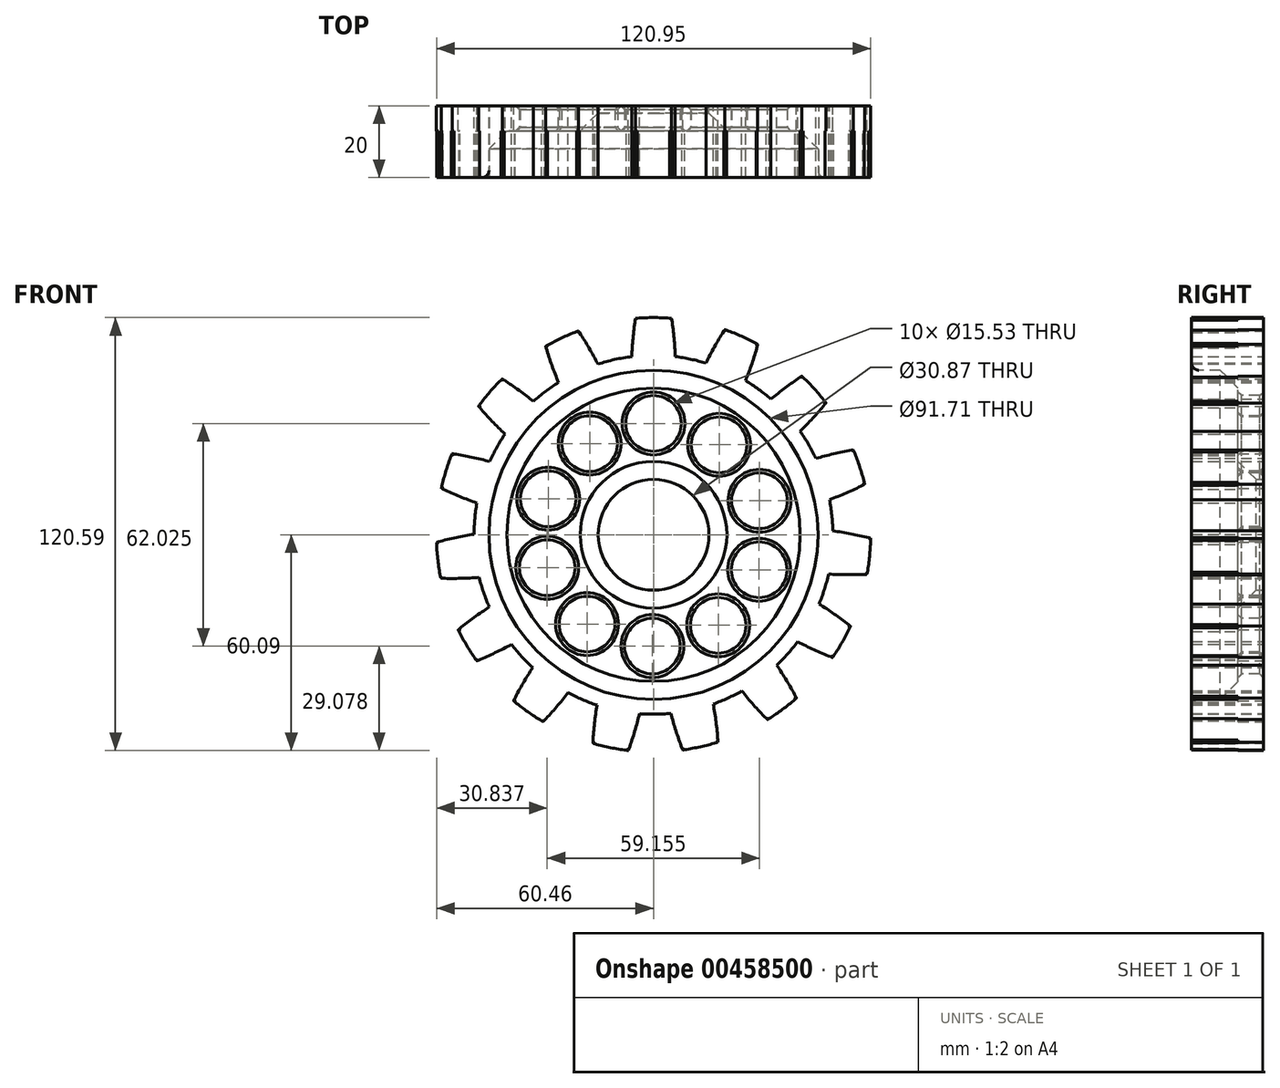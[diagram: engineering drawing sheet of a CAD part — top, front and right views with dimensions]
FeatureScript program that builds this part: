
annotation { "Feature Type Name" : "Feature", "Feature Type Description" : "" }
export const myFeature = defineFeature(function(context is Context, id is Id, definition is map)
    precondition{}
    {
        {
            var Q0;
            Q0=qCreatedBy(makeId("Front.planeOp"),FACE);
            var sketch = newSketch(context, id + "F0", { "sketchPlane" : qUnion([Q0])});
            skCircle(sketch, "E0", {"center": v(0, 0) * mm, "radius": 50 * mm});
            skArc(sketch, "E1", {"start": v(-2.05, -12.38) * mm, "mid": v(0, -12.55) * mm, "end": v(2.05, -12.38) * mm});
            skLineSegment(sketch, "E2.right", {"start": v(2.05, 10.3) * mm, "end": v(2.05, -12.38) * mm});
            skLineSegment(sketch, "E3.right", {"start": v(-2.05, 10.5) * mm, "end": v(-2.05, -12.38) * mm});
            skLineSegment(sketch, "E4", {"start": v(2.05, 10.3) * mm, "end": v(2.05, 12.38) * mm});
            skLineSegment(sketch, "E5", {"start": v(2.05, 12.38) * mm, "end": v(2.05, 10.3) * mm});
            skLineSegment(sketch, "E6", {"start": v(-2.05, 10.5) * mm, "end": v(-2.05, 12.38) * mm});
            skPoint(sketch, "E7.orphan", {"position": v(0, 10.5) * mm});
            skArc(sketch, "E8.trimOffspring", {"start": v(2.05, 12.38) * mm, "mid": v(0, 12.55) * mm, "end": v(-2.05, 12.38) * mm});
            skLineSegment(sketch, "E9.1.0", {"start": v(-7.83, 7.29) * mm, "end": v(5.62, -11.22) * mm});
            skLineSegment(sketch, "E9.1.1", {"start": v(-7.83, 7.29) * mm, "end": v(-8.94, 8.81) * mm});
            skArc(sketch, "E9.1.2", {"start": v(-5.62, 11.22) * mm, "mid": v(-7.38, 10.15) * mm, "end": v(-8.94, 8.81) * mm});
            skLineSegment(sketch, "E9.1.3", {"start": v(-4.4, 9.54) * mm, "end": v(8.94, -8.81) * mm});
            skLineSegment(sketch, "E9.1.4", {"start": v(-5.62, 11.22) * mm, "end": v(-4.4, 9.54) * mm});
            skArc(sketch, "E9.1.5", {"start": v(5.62, -11.22) * mm, "mid": v(7.38, -10.15) * mm, "end": v(8.94, -8.81) * mm});
            skLineSegment(sketch, "E9.2.0", {"start": v(-10.62, 1.3) * mm, "end": v(11.14, -5.78) * mm});
            skLineSegment(sketch, "E9.2.1", {"start": v(-10.62, 1.3) * mm, "end": v(-12.4, 1.88) * mm});
            skArc(sketch, "E9.2.2", {"start": v(-11.14, 5.78) * mm, "mid": v(-11.94, 3.88) * mm, "end": v(-12.4, 1.88) * mm});
            skLineSegment(sketch, "E9.2.3", {"start": v(-9.16, 5.13) * mm, "end": v(12.4, -1.88) * mm});
            skLineSegment(sketch, "E9.2.4", {"start": v(-11.14, 5.78) * mm, "end": v(-9.16, 5.13) * mm});
            skArc(sketch, "E9.2.5", {"start": v(11.14, -5.78) * mm, "mid": v(11.94, -3.88) * mm, "end": v(12.4, -1.88) * mm});
            skLineSegment(sketch, "E9.3.0", {"start": v(-9.35, -5.2) * mm, "end": v(12.4, 1.88) * mm});
            skLineSegment(sketch, "E9.3.1", {"start": v(-9.35, -5.2) * mm, "end": v(-11.14, -5.78) * mm});
            skArc(sketch, "E9.3.2", {"start": v(-12.4, -1.88) * mm, "mid": v(-11.94, -3.88) * mm, "end": v(-11.14, -5.78) * mm});
            skLineSegment(sketch, "E9.3.3", {"start": v(-10.43, -1.23) * mm, "end": v(11.14, 5.78) * mm});
            skLineSegment(sketch, "E9.3.4", {"start": v(-12.4, -1.88) * mm, "end": v(-10.43, -1.23) * mm});
            skArc(sketch, "E9.3.5", {"start": v(12.4, 1.88) * mm, "mid": v(11.94, 3.88) * mm, "end": v(11.14, 5.78) * mm});
            skLineSegment(sketch, "E9.4.0", {"start": v(-4.51, -9.7) * mm, "end": v(8.94, 8.81) * mm});
            skLineSegment(sketch, "E9.4.1", {"start": v(-4.51, -9.7) * mm, "end": v(-5.62, -11.22) * mm});
            skArc(sketch, "E9.4.2", {"start": v(-8.94, -8.81) * mm, "mid": v(-7.38, -10.15) * mm, "end": v(-5.62, -11.22) * mm});
            skLineSegment(sketch, "E9.4.3", {"start": v(-7.71, -7.13) * mm, "end": v(5.62, 11.22) * mm});
            skLineSegment(sketch, "E9.4.4", {"start": v(-8.94, -8.81) * mm, "end": v(-7.71, -7.13) * mm});
            skArc(sketch, "E9.4.5", {"start": v(8.94, 8.81) * mm, "mid": v(7.38, 10.15) * mm, "end": v(5.62, 11.22) * mm});
            skLineSegment(sketch, "E9.5.0", {"start": v(2.05, -10.5) * mm, "end": v(2.05, 12.38) * mm});
            skLineSegment(sketch, "E9.5.1", {"start": v(2.05, -10.5) * mm, "end": v(2.05, -12.38) * mm});
            skLineSegment(sketch, "E9.5.3", {"start": v(-2.05, -10.3) * mm, "end": v(-2.05, 12.38) * mm});
            skLineSegment(sketch, "E9.5.4", {"start": v(-2.05, -12.38) * mm, "end": v(-2.05, -10.3) * mm});
            skLineSegment(sketch, "E9.6.0", {"start": v(7.83, -7.29) * mm, "end": v(-5.62, 11.22) * mm});
            skLineSegment(sketch, "E9.6.1", {"start": v(7.83, -7.29) * mm, "end": v(8.94, -8.81) * mm});
            skArc(sketch, "E9.6.2", {"start": v(5.62, -11.22) * mm, "mid": v(7.38, -10.15) * mm, "end": v(8.94, -8.81) * mm});
            skLineSegment(sketch, "E9.6.3", {"start": v(4.4, -9.54) * mm, "end": v(-8.94, 8.81) * mm});
            skLineSegment(sketch, "E9.6.4", {"start": v(5.62, -11.22) * mm, "end": v(4.4, -9.54) * mm});
            skArc(sketch, "E9.6.5", {"start": v(-5.62, 11.22) * mm, "mid": v(-7.38, 10.15) * mm, "end": v(-8.94, 8.81) * mm});
            skLineSegment(sketch, "E9.7.0", {"start": v(10.62, -1.3) * mm, "end": v(-11.14, 5.78) * mm});
            skLineSegment(sketch, "E9.7.1", {"start": v(10.62, -1.3) * mm, "end": v(12.4, -1.88) * mm});
            skArc(sketch, "E9.7.2", {"start": v(11.14, -5.78) * mm, "mid": v(11.94, -3.88) * mm, "end": v(12.4, -1.88) * mm});
            skLineSegment(sketch, "E9.7.3", {"start": v(9.16, -5.13) * mm, "end": v(-12.4, 1.88) * mm});
            skLineSegment(sketch, "E9.7.4", {"start": v(11.14, -5.78) * mm, "end": v(9.16, -5.13) * mm});
            skArc(sketch, "E9.7.5", {"start": v(-11.14, 5.78) * mm, "mid": v(-11.94, 3.88) * mm, "end": v(-12.4, 1.88) * mm});
            skLineSegment(sketch, "E9.8.0", {"start": v(9.35, 5.2) * mm, "end": v(-12.4, -1.88) * mm});
            skLineSegment(sketch, "E9.8.1", {"start": v(9.35, 5.2) * mm, "end": v(11.14, 5.78) * mm});
            skArc(sketch, "E9.8.2", {"start": v(12.4, 1.88) * mm, "mid": v(11.94, 3.88) * mm, "end": v(11.14, 5.78) * mm});
            skLineSegment(sketch, "E9.8.3", {"start": v(10.43, 1.23) * mm, "end": v(-11.14, -5.78) * mm});
            skLineSegment(sketch, "E9.8.4", {"start": v(12.4, 1.88) * mm, "end": v(10.43, 1.23) * mm});
            skArc(sketch, "E9.8.5", {"start": v(-12.4, -1.88) * mm, "mid": v(-11.94, -3.88) * mm, "end": v(-11.14, -5.78) * mm});
            skLineSegment(sketch, "E9.9.0", {"start": v(4.51, 9.7) * mm, "end": v(-8.94, -8.81) * mm});
            skLineSegment(sketch, "E9.9.1", {"start": v(4.51, 9.7) * mm, "end": v(5.62, 11.22) * mm});
            skArc(sketch, "E9.9.2", {"start": v(8.94, 8.81) * mm, "mid": v(7.38, 10.15) * mm, "end": v(5.62, 11.22) * mm});
            skLineSegment(sketch, "E9.9.3", {"start": v(7.71, 7.13) * mm, "end": v(-5.62, -11.22) * mm});
            skLineSegment(sketch, "E9.9.4", {"start": v(8.94, 8.81) * mm, "end": v(7.71, 7.13) * mm});
            skArc(sketch, "E9.9.5", {"start": v(-8.94, -8.81) * mm, "mid": v(-7.38, -10.15) * mm, "end": v(-5.62, -11.22) * mm});
            skLineSegment(sketch, "E10", {"start": v(0, 50) * mm, "end": v(0, 46.5) * mm, "construction": true});
            skLineSegment(sketch, "E11", {"start": v(0, 46.5) * mm, "end": v(83.9, 46.5) * mm, "construction": true});
            skArc(sketch, "E12", {"start": v(-5.04, 60.29) * mm, "mid": v(-5.7, 54.98) * mm, "end": v(-6.05, 49.63) * mm});
            skArc(sketch, "E13", {"start": v(5.04, 60.29) * mm, "mid": v(0, 60.5) * mm, "end": v(-5.04, 60.29) * mm});
            skArc(sketch, "E14.MirrorC", {"start": v(5.04, 60.29) * mm, "mid": v(5.83, 53.42) * mm, "end": v(6.1, 46.5) * mm});
            skArc(sketch, "E15.trimOffspring", {"start": v(-6.8, 0.06) * mm, "mid": v(-6.85, -0.01) * mm, "end": v(-6.9, -0.08) * mm});
            skArc(sketch, "E16.trimOffspring", {"start": v(4.73, 3.7) * mm, "mid": v(4.84, 3.5) * mm, "end": v(4.94, 3.31) * mm});
            skArc(sketch, "E17.trimOffspring", {"start": v(6.8, 0.06) * mm, "mid": v(6.85, -0.01) * mm, "end": v(6.9, -0.08) * mm});
            skArc(sketch, "E18.1.0", {"start": v(29.06, 53.07) * mm, "mid": v(24.54, 55.3) * mm, "end": v(19.85, 57.15) * mm});
            skArc(sketch, "E18.1.1", {"start": v(19.85, 57.15) * mm, "mid": v(17.09, 52.56) * mm, "end": v(14.6, 47.82) * mm});
            skArc(sketch, "E18.1.2", {"start": v(29.06, 53.07) * mm, "mid": v(27, 46.46) * mm, "end": v(24.44, 40.03) * mm});
            skArc(sketch, "E18.2.0", {"start": v(48.08, 36.72) * mm, "mid": v(44.86, 40.6) * mm, "end": v(41.32, 44.19) * mm});
            skArc(sketch, "E18.2.1", {"start": v(41.32, 44.19) * mm, "mid": v(36.94, 41.11) * mm, "end": v(32.75, 37.79) * mm});
            skArc(sketch, "E18.2.2", {"start": v(48.08, 36.72) * mm, "mid": v(43.52, 31.52) * mm, "end": v(38.57, 26.68) * mm});
            skArc(sketch, "E18.3.0", {"start": v(58.84, 14.06) * mm, "mid": v(57.47, 18.91) * mm, "end": v(55.7, 23.63) * mm});
            skArc(sketch, "E18.3.1", {"start": v(55.7, 23.63) * mm, "mid": v(50.44, 22.6) * mm, "end": v(45.26, 21.26) * mm});
            skArc(sketch, "E18.3.2", {"start": v(58.84, 14.06) * mm, "mid": v(52.56, 11.15) * mm, "end": v(46.08, 8.74) * mm});
            skArc(sketch, "E18.4.0", {"start": v(59.49, -11.02) * mm, "mid": v(60.2, -6.02) * mm, "end": v(60.5, -1) * mm});
            skArc(sketch, "E18.4.1", {"start": v(60.5, -1) * mm, "mid": v(55.27, 0.2) * mm, "end": v(49.99, 1.07) * mm});
            skArc(sketch, "E18.4.2", {"start": v(59.49, -11.02) * mm, "mid": v(52.57, -11.12) * mm, "end": v(45.66, -10.7) * mm});
            skArc(sketch, "E18.5.0", {"start": v(49.9, -34.2) * mm, "mid": v(52.58, -29.92) * mm, "end": v(54.9, -25.44) * mm});
            skArc(sketch, "E18.5.1", {"start": v(54.9, -25.44) * mm, "mid": v(50.6, -22.24) * mm, "end": v(46.13, -19.3) * mm});
            skArc(sketch, "E18.5.2", {"start": v(49.9, -34.2) * mm, "mid": v(43.54, -31.49) * mm, "end": v(37.4, -28.3) * mm});
            skArc(sketch, "E18.6.0", {"start": v(31.75, -51.5) * mm, "mid": v(35.93, -48.68) * mm, "end": v(39.85, -45.52) * mm});
            skArc(sketch, "E18.6.1", {"start": v(39.85, -45.52) * mm, "mid": v(37.23, -40.85) * mm, "end": v(34.34, -36.34) * mm});
            skArc(sketch, "E18.6.2", {"start": v(31.75, -51.5) * mm, "mid": v(27.03, -46.44) * mm, "end": v(22.7, -41.04) * mm});
            skArc(sketch, "E18.7.0", {"start": v(8.13, -59.95) * mm, "mid": v(13.1, -59.07) * mm, "end": v(17.97, -57.77) * mm});
            skArc(sketch, "E18.7.1", {"start": v(17.97, -57.77) * mm, "mid": v(17.46, -52.44) * mm, "end": v(16.64, -47.15) * mm});
            skArc(sketch, "E18.7.2", {"start": v(8.13, -59.95) * mm, "mid": v(5.87, -53.41) * mm, "end": v(4.1, -46.72) * mm});
            skArc(sketch, "E18.8.0", {"start": v(-16.88, -58.1) * mm, "mid": v(-11.99, -59.3) * mm, "end": v(-7, -60.1) * mm});
            skArc(sketch, "E18.8.1", {"start": v(-7, -60.1) * mm, "mid": v(-5.3, -55.02) * mm, "end": v(-3.9, -49.85) * mm});
            skArc(sketch, "E18.8.2", {"start": v(-16.88, -58.1) * mm, "mid": v(-16.3, -51.2) * mm, "end": v(-15.2, -44.37) * mm});
            skArc(sketch, "E18.9.0", {"start": v(-39, -46.26) * mm, "mid": v(-35, -49.34) * mm, "end": v(-30.78, -52.09) * mm});
            skArc(sketch, "E18.9.1", {"start": v(-30.78, -52.09) * mm, "mid": v(-27.16, -48.14) * mm, "end": v(-23.8, -43.98) * mm});
            skArc(sketch, "E18.9.2", {"start": v(-39, -46.26) * mm, "mid": v(-35.67, -40.19) * mm, "end": v(-31.88, -34.4) * mm});
            skArc(sketch, "E18.10.0", {"start": v(-54.4, -26.46) * mm, "mid": v(-52.01, -30.9) * mm, "end": v(-49.26, -35.12) * mm});
            skArc(sketch, "E18.10.1", {"start": v(-49.26, -35.12) * mm, "mid": v(-44.35, -32.98) * mm, "end": v(-39.58, -30.55) * mm});
            skArc(sketch, "E18.10.2", {"start": v(-54.4, -26.46) * mm, "mid": v(-48.9, -22.27) * mm, "end": v(-43.1, -18.5) * mm});
            skArc(sketch, "E18.11.0", {"start": v(-60.46, -2.12) * mm, "mid": v(-60.08, -7.15) * mm, "end": v(-59.27, -12.13) * mm});
            skArc(sketch, "E18.11.1", {"start": v(-59.27, -12.13) * mm, "mid": v(-53.92, -12.16) * mm, "end": v(-48.57, -11.87) * mm});
            skArc(sketch, "E18.11.2", {"start": v(-60.46, -2.12) * mm, "mid": v(-53.73, -0.52) * mm, "end": v(-46.9, 0.56) * mm});
            skArc(sketch, "E18.12.0", {"start": v(-56.13, 22.58) * mm, "mid": v(-57.81, 17.83) * mm, "end": v(-59.1, 12.96) * mm});
            skArc(sketch, "E18.12.1", {"start": v(-59.1, 12.96) * mm, "mid": v(-54.21, 10.76) * mm, "end": v(-49.21, 8.85) * mm});
            skArc(sketch, "E18.12.2", {"start": v(-56.13, 22.58) * mm, "mid": v(-49.32, 21.32) * mm, "end": v(-42.64, 19.54) * mm});
            skArc(sketch, "E18.13.0", {"start": v(-42.14, 43.4) * mm, "mid": v(-45.61, 39.75) * mm, "end": v(-48.76, 35.81) * mm});
            skArc(sketch, "E18.13.1", {"start": v(-48.76, 35.81) * mm, "mid": v(-45.2, 31.82) * mm, "end": v(-41.39, 28.05) * mm});
            skArc(sketch, "E18.13.2", {"start": v(-42.14, 43.4) * mm, "mid": v(-36.44, 39.5) * mm, "end": v(-31.05, 35.15) * mm});
            skArc(sketch, "E18.14.0", {"start": v(-20.91, 56.77) * mm, "mid": v(-25.57, 54.83) * mm, "end": v(-30.04, 52.51) * mm});
            skArc(sketch, "E18.14.1", {"start": v(-30.04, 52.51) * mm, "mid": v(-28.4, 47.42) * mm, "end": v(-26.45, 42.43) * mm});
            skArc(sketch, "E18.14.2", {"start": v(-20.91, 56.77) * mm, "mid": v(-17.29, 50.88) * mm, "end": v(-14.12, 44.72) * mm});
            skLineSegment(sketch, "E18.anchor1", {"start": v(0, 0) * mm, "end": v(-5.04, 60.29) * mm, "construction": true});
            skLineSegment(sketch, "E18.anchor2", {"start": v(0, 0) * mm, "end": v(-30.04, 52.51) * mm, "construction": true});
            skCircle(sketch, "E19", {"center": v(0, 0) * mm, "radius": 10.5 * mm});
            skCircle(sketch, "E20", {"center": v(0, 0) * mm, "radius": 15.43 * mm});
            skSolve(sketch);
        }
        {
            var Q0;
            {var subQ0=sQuery(id+"F0.wireOp",EDGE,"E12");Q0=makeQuery(id+"F0.imprint","IMPRINT",FACE,{"disambiguationData":[TD([[makeQuery(id+"F0.imprint","IMPRINT",EDGE,{"derivedFrom":subQ0}),1.0]])]});}
            var Q1;
            {var subQ4=sQuery(id+"F0.wireOp",EDGE,"E18.14.0");Q1=makeQuery(id+"F0.imprint","IMPRINT",FACE,{"disambiguationData":[TD([[makeQuery(id+"F0.imprint","IMPRINT",EDGE,{"derivedFrom":subQ4}),1.0]])]});}
            var Q2;
            {var subQ4=sQuery(id+"F0.wireOp",EDGE,"E18.13.0");Q2=makeQuery(id+"F0.imprint","IMPRINT",FACE,{"disambiguationData":[TD([[makeQuery(id+"F0.imprint","IMPRINT",EDGE,{"derivedFrom":subQ4}),1.0]])]});}
            var Q3;
            {var subQ4=sQuery(id+"F0.wireOp",EDGE,"E18.12.0");Q3=makeQuery(id+"F0.imprint","IMPRINT",FACE,{"disambiguationData":[TD([[makeQuery(id+"F0.imprint","IMPRINT",EDGE,{"derivedFrom":subQ4}),1.0]])]});}
            var Q4;
            {var subQ4=sQuery(id+"F0.wireOp",EDGE,"E18.11.0");Q4=makeQuery(id+"F0.imprint","IMPRINT",FACE,{"disambiguationData":[TD([[makeQuery(id+"F0.imprint","IMPRINT",EDGE,{"derivedFrom":subQ4}),1.0]])]});}
            var Q5;
            {var subQ4=sQuery(id+"F0.wireOp",EDGE,"E18.10.0");Q5=makeQuery(id+"F0.imprint","IMPRINT",FACE,{"disambiguationData":[TD([[makeQuery(id+"F0.imprint","IMPRINT",EDGE,{"derivedFrom":subQ4}),1.0]])]});}
            var Q6;
            {var subQ4=sQuery(id+"F0.wireOp",EDGE,"E18.9.0");Q6=makeQuery(id+"F0.imprint","IMPRINT",FACE,{"disambiguationData":[TD([[makeQuery(id+"F0.imprint","IMPRINT",EDGE,{"derivedFrom":subQ4}),1.0]])]});}
            var Q7;
            {var subQ4=sQuery(id+"F0.wireOp",EDGE,"E18.8.0");Q7=makeQuery(id+"F0.imprint","IMPRINT",FACE,{"disambiguationData":[TD([[makeQuery(id+"F0.imprint","IMPRINT",EDGE,{"derivedFrom":subQ4}),1.0]])]});}
            var Q8;
            {var subQ4=sQuery(id+"F0.wireOp",EDGE,"E18.7.0");Q8=makeQuery(id+"F0.imprint","IMPRINT",FACE,{"disambiguationData":[TD([[makeQuery(id+"F0.imprint","IMPRINT",EDGE,{"derivedFrom":subQ4}),1.0]])]});}
            var Q9;
            {var subQ4=sQuery(id+"F0.wireOp",EDGE,"E18.5.0");Q9=makeQuery(id+"F0.imprint","IMPRINT",FACE,{"disambiguationData":[TD([[makeQuery(id+"F0.imprint","IMPRINT",EDGE,{"derivedFrom":subQ4}),1.0]])]});}
            var Q10;
            {var subQ4=sQuery(id+"F0.wireOp",EDGE,"E18.4.0");Q10=makeQuery(id+"F0.imprint","IMPRINT",FACE,{"disambiguationData":[TD([[makeQuery(id+"F0.imprint","IMPRINT",EDGE,{"derivedFrom":subQ4}),1.0]])]});}
            var Q11;
            {var subQ4=sQuery(id+"F0.wireOp",EDGE,"E18.3.0");Q11=makeQuery(id+"F0.imprint","IMPRINT",FACE,{"disambiguationData":[TD([[makeQuery(id+"F0.imprint","IMPRINT",EDGE,{"derivedFrom":subQ4}),1.0]])]});}
            var Q12;
            {var subQ4=sQuery(id+"F0.wireOp",EDGE,"E18.2.0");Q12=makeQuery(id+"F0.imprint","IMPRINT",FACE,{"disambiguationData":[TD([[makeQuery(id+"F0.imprint","IMPRINT",EDGE,{"derivedFrom":subQ4}),1.0]])]});}
            var Q13;
            {var subQ4=sQuery(id+"F0.wireOp",EDGE,"E18.1.0");Q13=makeQuery(id+"F0.imprint","IMPRINT",FACE,{"disambiguationData":[TD([[makeQuery(id+"F0.imprint","IMPRINT",EDGE,{"derivedFrom":subQ4}),1.0]])]});}
            var Q14;
            {var subQ4=sQuery(id+"F0.wireOp",EDGE,"E18.6.0");Q14=makeQuery(id+"F0.imprint","IMPRINT",FACE,{"disambiguationData":[TD([[makeQuery(id+"F0.imprint","IMPRINT",EDGE,{"derivedFrom":subQ4}),1.0]])]});}
            var Q15;
            {var subQ8=sQuery(id+"F0.wireOp",EDGE,"E9.5.1");Q15=makeQuery(id+"F0.imprint","IMPRINT",FACE,{"disambiguationData":[TD([[makeQuery(id+"F0.imprint","IMPRINT",EDGE,{"derivedFrom":subQ8}),1.0]])]});}
            var Q16;
            Q16=makeQuery(id+"F0.imprint","IMPRINT",FACE,{"disambiguationData":[TD([[makeQuery(id+"F0.imprint","IMPRINT",EDGE,{"derivedFrom":sQuery(id+"F0.wireOp",EDGE,"E20")}),-1.0]])]});
            extrude(context, id + "F1", {"entities" : qUnion([Q0, Q1, Q2, Q3, Q4, Q5, Q6, Q7, Q8, Q9, Q10, Q11, Q12, Q13, Q14, Q15, Q16]), "depth" : 20 * mm});
        }
        {
            var Q0;
            Q0=makeQuery(id+"F1.opExtrude","SWEPT_EDGE",EDGE,{"disambiguationData":[OSD([sQuery(id+"F0.wireOp",EDGE,"E12"),sQuery(id+"F0.wireOp",EDGE,"E13")])]});
            var Q1;
            Q1=makeQuery(id+"F1.opExtrude","SWEPT_EDGE",EDGE,{"disambiguationData":[OSD([sQuery(id+"F0.wireOp",EDGE,"E13"),sQuery(id+"F0.wireOp",EDGE,"E14.MirrorC")])]});
            var Q2;
            Q2=makeQuery(id+"F1.opExtrude","SWEPT_EDGE",EDGE,{"disambiguationData":[OSD([sQuery(id+"F0.wireOp",EDGE,"E18.14.0"),sQuery(id+"F0.wireOp",EDGE,"E18.14.2")])]});
            var Q3;
            Q3=makeQuery(id+"F1.opExtrude","SWEPT_EDGE",EDGE,{"disambiguationData":[OSD([sQuery(id+"F0.wireOp",EDGE,"E18.14.0"),sQuery(id+"F0.wireOp",EDGE,"E18.14.1")])]});
            var Q4;
            Q4=makeQuery(id+"F1.opExtrude","SWEPT_EDGE",EDGE,{"disambiguationData":[OSD([sQuery(id+"F0.wireOp",EDGE,"E18.13.0"),sQuery(id+"F0.wireOp",EDGE,"E18.13.2")])]});
            var Q5;
            Q5=makeQuery(id+"F1.opExtrude","SWEPT_EDGE",EDGE,{"disambiguationData":[OSD([sQuery(id+"F0.wireOp",EDGE,"E18.13.0"),sQuery(id+"F0.wireOp",EDGE,"E18.13.1")])]});
            var Q6;
            Q6=makeQuery(id+"F1.opExtrude","SWEPT_EDGE",EDGE,{"disambiguationData":[OSD([sQuery(id+"F0.wireOp",EDGE,"E18.12.0"),sQuery(id+"F0.wireOp",EDGE,"E18.12.2")])]});
            var Q7;
            Q7=makeQuery(id+"F1.opExtrude","SWEPT_EDGE",EDGE,{"disambiguationData":[OSD([sQuery(id+"F0.wireOp",EDGE,"E18.12.0"),sQuery(id+"F0.wireOp",EDGE,"E18.12.1")])]});
            var Q8;
            Q8=makeQuery(id+"F1.opExtrude","SWEPT_EDGE",EDGE,{"disambiguationData":[OSD([sQuery(id+"F0.wireOp",EDGE,"E18.1.0"),sQuery(id+"F0.wireOp",EDGE,"E18.1.1")])]});
            var Q9;
            Q9=makeQuery(id+"F1.opExtrude","SWEPT_EDGE",EDGE,{"disambiguationData":[OSD([sQuery(id+"F0.wireOp",EDGE,"E18.1.0"),sQuery(id+"F0.wireOp",EDGE,"E18.1.2")])]});
            var Q10;
            Q10=makeQuery(id+"F1.opExtrude","SWEPT_EDGE",EDGE,{"disambiguationData":[OSD([sQuery(id+"F0.wireOp",EDGE,"E18.2.0"),sQuery(id+"F0.wireOp",EDGE,"E18.2.1")])]});
            var Q11;
            Q11=makeQuery(id+"F1.opExtrude","SWEPT_EDGE",EDGE,{"disambiguationData":[OSD([sQuery(id+"F0.wireOp",EDGE,"E18.2.0"),sQuery(id+"F0.wireOp",EDGE,"E18.2.2")])]});
            var Q12;
            Q12=makeQuery(id+"F1.opExtrude","SWEPT_EDGE",EDGE,{"disambiguationData":[OSD([sQuery(id+"F0.wireOp",EDGE,"E18.3.0"),sQuery(id+"F0.wireOp",EDGE,"E18.3.1")])]});
            var Q13;
            Q13=makeQuery(id+"F1.opExtrude","SWEPT_EDGE",EDGE,{"disambiguationData":[OSD([sQuery(id+"F0.wireOp",EDGE,"E18.3.0"),sQuery(id+"F0.wireOp",EDGE,"E18.3.2")])]});
            var Q14;
            Q14=makeQuery(id+"F1.opExtrude","SWEPT_EDGE",EDGE,{"disambiguationData":[OSD([sQuery(id+"F0.wireOp",EDGE,"E18.4.0"),sQuery(id+"F0.wireOp",EDGE,"E18.4.1")])]});
            var Q15;
            Q15=makeQuery(id+"F1.opExtrude","SWEPT_EDGE",EDGE,{"disambiguationData":[OSD([sQuery(id+"F0.wireOp",EDGE,"E18.4.0"),sQuery(id+"F0.wireOp",EDGE,"E18.4.2")])]});
            var Q16;
            Q16=makeQuery(id+"F1.opExtrude","SWEPT_EDGE",EDGE,{"disambiguationData":[OSD([sQuery(id+"F0.wireOp",EDGE,"E18.5.0"),sQuery(id+"F0.wireOp",EDGE,"E18.5.1")])]});
            var Q17;
            Q17=makeQuery(id+"F1.opExtrude","SWEPT_EDGE",EDGE,{"disambiguationData":[OSD([sQuery(id+"F0.wireOp",EDGE,"E18.5.0"),sQuery(id+"F0.wireOp",EDGE,"E18.5.2")])]});
            var Q18;
            Q18=makeQuery(id+"F1.opExtrude","SWEPT_EDGE",EDGE,{"disambiguationData":[OSD([sQuery(id+"F0.wireOp",EDGE,"E18.6.0"),sQuery(id+"F0.wireOp",EDGE,"E18.6.1")])]});
            var Q19;
            Q19=makeQuery(id+"F1.opExtrude","SWEPT_EDGE",EDGE,{"disambiguationData":[OSD([sQuery(id+"F0.wireOp",EDGE,"E18.6.0"),sQuery(id+"F0.wireOp",EDGE,"E18.6.2")])]});
            var Q20;
            Q20=makeQuery(id+"F1.opExtrude","SWEPT_EDGE",EDGE,{"disambiguationData":[OSD([sQuery(id+"F0.wireOp",EDGE,"E18.7.0"),sQuery(id+"F0.wireOp",EDGE,"E18.7.1")])]});
            var Q21;
            Q21=makeQuery(id+"F1.opExtrude","SWEPT_EDGE",EDGE,{"disambiguationData":[OSD([sQuery(id+"F0.wireOp",EDGE,"E18.7.0"),sQuery(id+"F0.wireOp",EDGE,"E18.7.2")])]});
            var Q22;
            Q22=makeQuery(id+"F1.opExtrude","SWEPT_EDGE",EDGE,{"disambiguationData":[OSD([sQuery(id+"F0.wireOp",EDGE,"E18.8.0"),sQuery(id+"F0.wireOp",EDGE,"E18.8.1")])]});
            var Q23;
            Q23=makeQuery(id+"F1.opExtrude","SWEPT_EDGE",EDGE,{"disambiguationData":[OSD([sQuery(id+"F0.wireOp",EDGE,"E18.8.0"),sQuery(id+"F0.wireOp",EDGE,"E18.8.2")])]});
            var Q24;
            Q24=makeQuery(id+"F1.opExtrude","SWEPT_EDGE",EDGE,{"disambiguationData":[OSD([sQuery(id+"F0.wireOp",EDGE,"E18.11.0"),sQuery(id+"F0.wireOp",EDGE,"E18.11.2")])]});
            var Q25;
            Q25=makeQuery(id+"F1.opExtrude","SWEPT_EDGE",EDGE,{"disambiguationData":[OSD([sQuery(id+"F0.wireOp",EDGE,"E18.11.0"),sQuery(id+"F0.wireOp",EDGE,"E18.11.1")])]});
            var Q26;
            Q26=makeQuery(id+"F1.opExtrude","SWEPT_EDGE",EDGE,{"disambiguationData":[OSD([sQuery(id+"F0.wireOp",EDGE,"E18.10.0"),sQuery(id+"F0.wireOp",EDGE,"E18.10.2")])]});
            var Q27;
            Q27=makeQuery(id+"F1.opExtrude","SWEPT_EDGE",EDGE,{"disambiguationData":[OSD([sQuery(id+"F0.wireOp",EDGE,"E18.10.0"),sQuery(id+"F0.wireOp",EDGE,"E18.10.1")])]});
            var Q28;
            Q28=makeQuery(id+"F1.opExtrude","SWEPT_EDGE",EDGE,{"disambiguationData":[OSD([sQuery(id+"F0.wireOp",EDGE,"E18.9.0"),sQuery(id+"F0.wireOp",EDGE,"E18.9.2")])]});
            var Q29;
            Q29=makeQuery(id+"F1.opExtrude","SWEPT_EDGE",EDGE,{"disambiguationData":[OSD([sQuery(id+"F0.wireOp",EDGE,"E18.9.0"),sQuery(id+"F0.wireOp",EDGE,"E18.9.1")])]});
            chamfer(context, id + "F2", {"entities" : qUnion([Q0, Q1, Q2, Q3, Q4, Q5, Q6, Q7, Q8, Q9, Q10, Q11, Q12, Q13, Q14, Q15, Q16, Q17, Q18, Q19, Q20, Q21, Q22, Q23, Q24, Q25, Q26, Q27, Q28, Q29]), "width" : 0.7 * mm, "tangentPropagation" : true});
        }
        {
            var Q0;
            Q0=qCreatedBy(makeId("Front.planeOp"),FACE);
            cPlane(context, id + "F3", {"entities" : qUnion([Q0]), "cplaneType" : CPlaneType.OFFSET, "offset" : 21 * mm, "width" : 150 * mm, "height" : 150 * mm});
        }
        {
            var Q0;
            Q0=qCreatedBy(id+"F3.planeOp",FACE);
            var sketch = newSketch(context, id + "F4", { "sketchPlane" : qUnion([Q0])});
            skCircle(sketch, "E21", {"center": v(0, 0) * mm, "radius": 45.85 * mm});
            skSolve(sketch);
        }
        {
            var Q0;
            Q0=makeQuery(id+"F4.imprint","IMPRINT",FACE,{"disambiguationData":[TD([[makeQuery(id+"F4.imprint","IMPRINT",EDGE,{"derivedFrom":sQuery(id+"F4.wireOp",EDGE,"E21")}),1.0]])]});
            extrude(context, id + "F5", {"entities" : qUnion([Q0]), "operationType" : NewBodyOperationType.REMOVE, "oppositeDirection" : true, "depth" : 17 * mm});
        }
        {
            var Q0;
            Q0 = qSketchRegion(id + "F0", true);
            extrude(context, id + "F6", {"entities" : qUnion([Q0]), "operationType" : NewBodyOperationType.ADD, "depth" : 7 * mm});
        }
        {
            var Q0;
            {var subQ0=sQuery(id+"F0.wireOp",EDGE,"E20");Q0=makeQuery(id+"F6.boolean.opBoolean","SPLIT",FACE,{"disambiguationData":[TD([makeQuery(id+"F5.boolean.opBoolean","COPY",FACE,{"derivedFrom":makeQuery(id+"F5.opExtrude","SWEPT_FACE",FACE,{"disambiguationData":[OSD([sQuery(id+"F4.wireOp",EDGE,"E21")])]})})])],"derivedFrom":makeQuery(id+"F6.opExtrude","CAP_FACE",FACE,{"disambiguationData":[OSD([sQuery(id+"F0.wireOp",EDGE,"E0"),sQuery(id+"F0.wireOp",EDGE,"E12"),sQuery(id+"F0.wireOp",EDGE,"E13"),sQuery(id+"F0.wireOp",EDGE,"E14.MirrorC"),sQuery(id+"F0.wireOp",EDGE,"E18.1.0"),sQuery(id+"F0.wireOp",EDGE,"E18.1.1"),sQuery(id+"F0.wireOp",EDGE,"E18.1.2"),sQuery(id+"F0.wireOp",EDGE,"E18.2.0"),sQuery(id+"F0.wireOp",EDGE,"E18.2.1"),sQuery(id+"F0.wireOp",EDGE,"E18.2.2"),sQuery(id+"F0.wireOp",EDGE,"E18.3.0"),sQuery(id+"F0.wireOp",EDGE,"E18.3.1"),sQuery(id+"F0.wireOp",EDGE,"E18.3.2"),sQuery(id+"F0.wireOp",EDGE,"E18.4.0"),sQuery(id+"F0.wireOp",EDGE,"E18.4.1"),sQuery(id+"F0.wireOp",EDGE,"E18.4.2"),sQuery(id+"F0.wireOp",EDGE,"E18.5.0"),sQuery(id+"F0.wireOp",EDGE,"E18.5.1"),sQuery(id+"F0.wireOp",EDGE,"E18.5.2"),sQuery(id+"F0.wireOp",EDGE,"E18.6.0"),sQuery(id+"F0.wireOp",EDGE,"E18.6.1"),sQuery(id+"F0.wireOp",EDGE,"E18.6.2"),sQuery(id+"F0.wireOp",EDGE,"E18.7.0"),sQuery(id+"F0.wireOp",EDGE,"E18.7.1"),sQuery(id+"F0.wireOp",EDGE,"E18.7.2"),sQuery(id+"F0.wireOp",EDGE,"E18.8.0"),sQuery(id+"F0.wireOp",EDGE,"E18.8.1"),sQuery(id+"F0.wireOp",EDGE,"E18.8.2"),sQuery(id+"F0.wireOp",EDGE,"E18.9.0"),sQuery(id+"F0.wireOp",EDGE,"E18.9.1"),sQuery(id+"F0.wireOp",EDGE,"E18.9.2"),sQuery(id+"F0.wireOp",EDGE,"E18.10.0"),sQuery(id+"F0.wireOp",EDGE,"E18.10.1"),sQuery(id+"F0.wireOp",EDGE,"E18.10.2"),sQuery(id+"F0.wireOp",EDGE,"E18.11.0"),sQuery(id+"F0.wireOp",EDGE,"E18.11.1"),sQuery(id+"F0.wireOp",EDGE,"E18.11.2"),sQuery(id+"F0.wireOp",EDGE,"E18.12.0"),sQuery(id+"F0.wireOp",EDGE,"E18.12.1"),sQuery(id+"F0.wireOp",EDGE,"E18.12.2"),sQuery(id+"F0.wireOp",EDGE,"E18.13.0"),sQuery(id+"F0.wireOp",EDGE,"E18.13.1"),sQuery(id+"F0.wireOp",EDGE,"E18.13.2"),sQuery(id+"F0.wireOp",EDGE,"E18.14.0"),sQuery(id+"F0.wireOp",EDGE,"E18.14.1"),sQuery(id+"F0.wireOp",EDGE,"E18.14.2"),subQ0])],"isStart":false})});}
            chamfer(context, id + "F7", {"entities" : qUnion([Q0]), "width" : 5 * mm, "tangentPropagation" : true});
        }
        {
            var Q0;
            Q0=makeQuery(id+"F5.boolean.opBoolean","INTERSECT",EDGE,{"derivedFrom":[makeQuery(id+"F1.opExtrude","CAP_FACE",FACE,{"disambiguationData":[OSD([sQuery(id+"F0.wireOp",EDGE,"E0"),sQuery(id+"F0.wireOp",EDGE,"E9.5.0"),sQuery(id+"F0.wireOp",EDGE,"E9.5.1"),sQuery(id+"F0.wireOp",EDGE,"E1"),sQuery(id+"F0.wireOp",EDGE,"E9.5.3"),sQuery(id+"F0.wireOp",EDGE,"E9.5.4"),sQuery(id+"F0.wireOp",EDGE,"E8.trimOffspring"),sQuery(id+"F0.wireOp",EDGE,"E9.6.0"),sQuery(id+"F0.wireOp",EDGE,"E9.6.1"),sQuery(id+"F0.wireOp",EDGE,"E9.6.2"),sQuery(id+"F0.wireOp",EDGE,"E9.6.3"),sQuery(id+"F0.wireOp",EDGE,"E9.6.4"),sQuery(id+"F0.wireOp",EDGE,"E9.6.5"),sQuery(id+"F0.wireOp",EDGE,"E9.7.0"),sQuery(id+"F0.wireOp",EDGE,"E9.7.1"),sQuery(id+"F0.wireOp",EDGE,"E9.7.2"),sQuery(id+"F0.wireOp",EDGE,"E9.7.3"),sQuery(id+"F0.wireOp",EDGE,"E9.7.4"),sQuery(id+"F0.wireOp",EDGE,"E9.7.5"),sQuery(id+"F0.wireOp",EDGE,"E9.8.0"),sQuery(id+"F0.wireOp",EDGE,"E9.8.1"),sQuery(id+"F0.wireOp",EDGE,"E9.8.2"),sQuery(id+"F0.wireOp",EDGE,"E9.8.3"),sQuery(id+"F0.wireOp",EDGE,"E9.8.4"),sQuery(id+"F0.wireOp",EDGE,"E9.8.5"),sQuery(id+"F0.wireOp",EDGE,"E9.9.0"),sQuery(id+"F0.wireOp",EDGE,"E9.9.1"),sQuery(id+"F0.wireOp",EDGE,"E9.9.2"),sQuery(id+"F0.wireOp",EDGE,"E9.9.3"),sQuery(id+"F0.wireOp",EDGE,"E9.9.4"),sQuery(id+"F0.wireOp",EDGE,"E9.9.5"),sQuery(id+"F0.wireOp",EDGE,"E12"),sQuery(id+"F0.wireOp",EDGE,"E13"),sQuery(id+"F0.wireOp",EDGE,"E14.MirrorC"),sQuery(id+"F0.wireOp",EDGE,"E18.1.0"),sQuery(id+"F0.wireOp",EDGE,"E18.1.1"),sQuery(id+"F0.wireOp",EDGE,"E18.1.2"),sQuery(id+"F0.wireOp",EDGE,"E18.2.0"),sQuery(id+"F0.wireOp",EDGE,"E18.2.1"),sQuery(id+"F0.wireOp",EDGE,"E18.2.2"),sQuery(id+"F0.wireOp",EDGE,"E18.3.0"),sQuery(id+"F0.wireOp",EDGE,"E18.3.1"),sQuery(id+"F0.wireOp",EDGE,"E18.3.2"),sQuery(id+"F0.wireOp",EDGE,"E18.4.0"),sQuery(id+"F0.wireOp",EDGE,"E18.4.1"),sQuery(id+"F0.wireOp",EDGE,"E18.4.2"),sQuery(id+"F0.wireOp",EDGE,"E18.5.0"),sQuery(id+"F0.wireOp",EDGE,"E18.5.1"),sQuery(id+"F0.wireOp",EDGE,"E18.5.2"),sQuery(id+"F0.wireOp",EDGE,"E18.6.0"),sQuery(id+"F0.wireOp",EDGE,"E18.6.1"),sQuery(id+"F0.wireOp",EDGE,"E18.6.2"),sQuery(id+"F0.wireOp",EDGE,"E18.7.0"),sQuery(id+"F0.wireOp",EDGE,"E18.7.1"),sQuery(id+"F0.wireOp",EDGE,"E18.7.2"),sQuery(id+"F0.wireOp",EDGE,"E18.8.0"),sQuery(id+"F0.wireOp",EDGE,"E18.8.1"),sQuery(id+"F0.wireOp",EDGE,"E18.8.2"),sQuery(id+"F0.wireOp",EDGE,"E18.9.0"),sQuery(id+"F0.wireOp",EDGE,"E18.9.1"),sQuery(id+"F0.wireOp",EDGE,"E18.9.2"),sQuery(id+"F0.wireOp",EDGE,"E18.10.0"),sQuery(id+"F0.wireOp",EDGE,"E18.10.1"),sQuery(id+"F0.wireOp",EDGE,"E18.10.2"),sQuery(id+"F0.wireOp",EDGE,"E18.11.0"),sQuery(id+"F0.wireOp",EDGE,"E18.11.1"),sQuery(id+"F0.wireOp",EDGE,"E18.11.2"),sQuery(id+"F0.wireOp",EDGE,"E18.12.0"),sQuery(id+"F0.wireOp",EDGE,"E18.12.1"),sQuery(id+"F0.wireOp",EDGE,"E18.12.2"),sQuery(id+"F0.wireOp",EDGE,"E18.13.0"),sQuery(id+"F0.wireOp",EDGE,"E18.13.1"),sQuery(id+"F0.wireOp",EDGE,"E18.13.2"),sQuery(id+"F0.wireOp",EDGE,"E18.14.0"),sQuery(id+"F0.wireOp",EDGE,"E18.14.1"),sQuery(id+"F0.wireOp",EDGE,"E18.14.2"),sQuery(id+"F0.wireOp",EDGE,"E19")])],"isStart":false}),makeQuery(id+"F5.opExtrude","SWEPT_FACE",FACE,{"disambiguationData":[OSD([sQuery(id+"F4.wireOp",EDGE,"E21")])]})]});
            fillet(context, id + "F8", {"entities" : qUnion([Q0]), "radius" : 2 * mm, "tangentPropagation" : true, "allowEdgeOverflow" : false});
        }
        {
            var Q0;
            Q0=qCreatedBy(id+"F3.planeOp",FACE);
            var sketch = newSketch(context, id + "F9", { "sketchPlane" : qUnion([Q0])});
            skCircle(sketch, "E22", {"center": v(0, 31.01) * mm, "radius": 7.76 * mm});
            skCircle(sketch, "E23.1.0", {"center": v(18.28, 25.05) * mm, "radius": 7.76 * mm});
            skCircle(sketch, "E23.2.0", {"center": v(29.53, 9.47) * mm, "radius": 7.76 * mm});
            skCircle(sketch, "E23.3.0", {"center": v(29.44, -9.76) * mm, "radius": 7.76 * mm});
            skCircle(sketch, "E23.4.0", {"center": v(18.03, -25.23) * mm, "radius": 7.76 * mm});
            skCircle(sketch, "E23.5.0", {"center": v(-0.3, -31.01) * mm, "radius": 7.76 * mm});
            skCircle(sketch, "E23.6.0", {"center": v(-18.52, -24.88) * mm, "radius": 7.76 * mm});
            skCircle(sketch, "E23.7.0", {"center": v(-29.62, -9.18) * mm, "radius": 7.76 * mm});
            skCircle(sketch, "E23.8.0", {"center": v(-29.34, 10.04) * mm, "radius": 7.76 * mm});
            skCircle(sketch, "E23.9.0", {"center": v(-17.79, 25.4) * mm, "radius": 7.76 * mm});
            skPoint(sketch, "E23.center", {"position": v(0, 0) * mm});
            skLineSegment(sketch, "E23.anchor1", {"start": v(0, 0) * mm, "end": v(0, 31.01) * mm, "construction": true});
            skLineSegment(sketch, "E23.anchor2", {"start": v(0, 0) * mm, "end": v(-17.79, 25.4) * mm, "construction": true});
            skSolve(sketch);
        }
        {
            var Q0;
            Q0=makeQuery(id+"F9.imprint","IMPRINT",FACE,{"disambiguationData":[TD([[makeQuery(id+"F9.imprint","IMPRINT",EDGE,{"derivedFrom":sQuery(id+"F9.wireOp",EDGE,"E23.9.0")}),1.0]])]});
            var Q1;
            Q1=makeQuery(id+"F9.imprint","IMPRINT",FACE,{"disambiguationData":[TD([[makeQuery(id+"F9.imprint","IMPRINT",EDGE,{"derivedFrom":sQuery(id+"F9.wireOp",EDGE,"E22")}),1.0]])]});
            var Q2;
            Q2=makeQuery(id+"F9.imprint","IMPRINT",FACE,{"disambiguationData":[TD([[makeQuery(id+"F9.imprint","IMPRINT",EDGE,{"derivedFrom":sQuery(id+"F9.wireOp",EDGE,"E23.1.0")}),1.0]])]});
            var Q3;
            Q3=makeQuery(id+"F9.imprint","IMPRINT",FACE,{"disambiguationData":[TD([[makeQuery(id+"F9.imprint","IMPRINT",EDGE,{"derivedFrom":sQuery(id+"F9.wireOp",EDGE,"E23.2.0")}),1.0]])]});
            var Q4;
            Q4=makeQuery(id+"F9.imprint","IMPRINT",FACE,{"disambiguationData":[TD([[makeQuery(id+"F9.imprint","IMPRINT",EDGE,{"derivedFrom":sQuery(id+"F9.wireOp",EDGE,"E23.3.0")}),1.0]])]});
            var Q5;
            Q5=makeQuery(id+"F9.imprint","IMPRINT",FACE,{"disambiguationData":[TD([[makeQuery(id+"F9.imprint","IMPRINT",EDGE,{"derivedFrom":sQuery(id+"F9.wireOp",EDGE,"E23.4.0")}),1.0]])]});
            var Q6;
            Q6=makeQuery(id+"F9.imprint","IMPRINT",FACE,{"disambiguationData":[TD([[makeQuery(id+"F9.imprint","IMPRINT",EDGE,{"derivedFrom":sQuery(id+"F9.wireOp",EDGE,"E23.5.0")}),1.0]])]});
            var Q7;
            Q7=makeQuery(id+"F9.imprint","IMPRINT",FACE,{"disambiguationData":[TD([[makeQuery(id+"F9.imprint","IMPRINT",EDGE,{"derivedFrom":sQuery(id+"F9.wireOp",EDGE,"E23.6.0")}),1.0]])]});
            var Q8;
            Q8=makeQuery(id+"F9.imprint","IMPRINT",FACE,{"disambiguationData":[TD([[makeQuery(id+"F9.imprint","IMPRINT",EDGE,{"derivedFrom":sQuery(id+"F9.wireOp",EDGE,"E23.7.0")}),1.0]])]});
            var Q9;
            Q9=makeQuery(id+"F9.imprint","IMPRINT",FACE,{"disambiguationData":[TD([[makeQuery(id+"F9.imprint","IMPRINT",EDGE,{"derivedFrom":sQuery(id+"F9.wireOp",EDGE,"E23.8.0")}),1.0]])]});
            extrude(context, id + "F10", {"entities" : qUnion([Q0, Q1, Q2, Q3, Q4, Q5, Q6, Q7, Q8, Q9]), "operationType" : NewBodyOperationType.REMOVE, "oppositeDirection" : true, "depth" : 25 * mm});
        }
        {
            var Q0;
            {var subQ0=sQuery(id+"F0.wireOp",EDGE,"E18.14.2");var subQ1=sQuery(id+"F0.wireOp",EDGE,"E18.14.1");var subQ2=sQuery(id+"F0.wireOp",EDGE,"E18.14.0");var subQ3=sQuery(id+"F0.wireOp",EDGE,"E18.13.2");var subQ4=sQuery(id+"F0.wireOp",EDGE,"E18.13.1");var subQ5=sQuery(id+"F0.wireOp",EDGE,"E18.13.0");var subQ6=sQuery(id+"F0.wireOp",EDGE,"E18.12.2");var subQ7=sQuery(id+"F0.wireOp",EDGE,"E18.12.1");var subQ8=sQuery(id+"F0.wireOp",EDGE,"E18.12.0");var subQ9=sQuery(id+"F0.wireOp",EDGE,"E18.11.2");var subQ10=sQuery(id+"F0.wireOp",EDGE,"E18.11.1");var subQ11=sQuery(id+"F0.wireOp",EDGE,"E18.11.0");var subQ12=sQuery(id+"F0.wireOp",EDGE,"E18.10.2");var subQ13=sQuery(id+"F0.wireOp",EDGE,"E18.10.1");var subQ14=sQuery(id+"F0.wireOp",EDGE,"E18.10.0");var subQ15=sQuery(id+"F0.wireOp",EDGE,"E18.9.2");var subQ16=sQuery(id+"F0.wireOp",EDGE,"E18.9.1");var subQ17=sQuery(id+"F0.wireOp",EDGE,"E18.9.0");var subQ18=sQuery(id+"F0.wireOp",EDGE,"E18.8.2");var subQ19=sQuery(id+"F0.wireOp",EDGE,"E18.8.1");var subQ20=sQuery(id+"F0.wireOp",EDGE,"E18.8.0");var subQ21=sQuery(id+"F0.wireOp",EDGE,"E18.7.2");var subQ22=sQuery(id+"F0.wireOp",EDGE,"E18.7.1");var subQ23=sQuery(id+"F0.wireOp",EDGE,"E18.7.0");var subQ24=sQuery(id+"F0.wireOp",EDGE,"E18.6.2");var subQ25=sQuery(id+"F0.wireOp",EDGE,"E18.6.1");var subQ26=sQuery(id+"F0.wireOp",EDGE,"E18.6.0");var subQ27=sQuery(id+"F0.wireOp",EDGE,"E18.5.2");var subQ28=sQuery(id+"F0.wireOp",EDGE,"E18.5.1");var subQ29=sQuery(id+"F0.wireOp",EDGE,"E18.5.0");var subQ30=sQuery(id+"F0.wireOp",EDGE,"E18.4.2");var subQ31=sQuery(id+"F0.wireOp",EDGE,"E18.4.1");var subQ32=sQuery(id+"F0.wireOp",EDGE,"E18.4.0");var subQ33=sQuery(id+"F0.wireOp",EDGE,"E18.3.2");var subQ34=sQuery(id+"F0.wireOp",EDGE,"E18.3.1");var subQ35=sQuery(id+"F0.wireOp",EDGE,"E18.3.0");var subQ36=sQuery(id+"F0.wireOp",EDGE,"E18.2.2");var subQ37=sQuery(id+"F0.wireOp",EDGE,"E18.2.1");var subQ38=sQuery(id+"F0.wireOp",EDGE,"E18.2.0");var subQ39=sQuery(id+"F0.wireOp",EDGE,"E18.1.2");var subQ40=sQuery(id+"F0.wireOp",EDGE,"E18.1.1");var subQ41=sQuery(id+"F0.wireOp",EDGE,"E18.1.0");var subQ42=sQuery(id+"F0.wireOp",EDGE,"E14.MirrorC");var subQ43=sQuery(id+"F0.wireOp",EDGE,"E13");var subQ44=sQuery(id+"F0.wireOp",EDGE,"E12");var subQ45=sQuery(id+"F0.wireOp",EDGE,"E0");Q0=makeQuery(id+"F10.boolean.opBoolean","INTERSECT",EDGE,{"derivedFrom":[makeQuery(id+"F6.boolean.opBoolean","MERGE",FACE,{"derivedFrom":[makeQuery(id+"F1.opExtrude","CAP_FACE",FACE,{"disambiguationData":[OSD([subQ45,sQuery(id+"F0.wireOp",EDGE,"E9.5.0"),sQuery(id+"F0.wireOp",EDGE,"E9.5.1"),sQuery(id+"F0.wireOp",EDGE,"E1"),sQuery(id+"F0.wireOp",EDGE,"E9.5.3"),sQuery(id+"F0.wireOp",EDGE,"E9.5.4"),sQuery(id+"F0.wireOp",EDGE,"E8.trimOffspring"),sQuery(id+"F0.wireOp",EDGE,"E9.6.0"),sQuery(id+"F0.wireOp",EDGE,"E9.6.1"),sQuery(id+"F0.wireOp",EDGE,"E9.6.2"),sQuery(id+"F0.wireOp",EDGE,"E9.6.3"),sQuery(id+"F0.wireOp",EDGE,"E9.6.4"),sQuery(id+"F0.wireOp",EDGE,"E9.6.5"),sQuery(id+"F0.wireOp",EDGE,"E9.7.0"),sQuery(id+"F0.wireOp",EDGE,"E9.7.1"),sQuery(id+"F0.wireOp",EDGE,"E9.7.2"),sQuery(id+"F0.wireOp",EDGE,"E9.7.3"),sQuery(id+"F0.wireOp",EDGE,"E9.7.4"),sQuery(id+"F0.wireOp",EDGE,"E9.7.5"),sQuery(id+"F0.wireOp",EDGE,"E9.8.0"),sQuery(id+"F0.wireOp",EDGE,"E9.8.1"),sQuery(id+"F0.wireOp",EDGE,"E9.8.2"),sQuery(id+"F0.wireOp",EDGE,"E9.8.3"),sQuery(id+"F0.wireOp",EDGE,"E9.8.4"),sQuery(id+"F0.wireOp",EDGE,"E9.8.5"),sQuery(id+"F0.wireOp",EDGE,"E9.9.0"),sQuery(id+"F0.wireOp",EDGE,"E9.9.1"),sQuery(id+"F0.wireOp",EDGE,"E9.9.2"),sQuery(id+"F0.wireOp",EDGE,"E9.9.3"),sQuery(id+"F0.wireOp",EDGE,"E9.9.4"),sQuery(id+"F0.wireOp",EDGE,"E9.9.5"),subQ44,subQ43,subQ42,subQ41,subQ40,subQ39,subQ38,subQ37,subQ36,subQ35,subQ34,subQ33,subQ32,subQ31,subQ30,subQ29,subQ28,subQ27,subQ26,subQ25,subQ24,subQ23,subQ22,subQ21,subQ20,subQ19,subQ18,subQ17,subQ16,subQ15,subQ14,subQ13,subQ12,subQ11,subQ10,subQ9,subQ8,subQ7,subQ6,subQ5,subQ4,subQ3,subQ2,subQ1,subQ0,sQuery(id+"F0.wireOp",EDGE,"E19")])],"isStart":true}),makeQuery(id+"F6.opExtrude","CAP_FACE",FACE,{"disambiguationData":[OSD([subQ45,subQ44,subQ43,subQ42,subQ41,subQ40,subQ39,subQ38,subQ37,subQ36,subQ35,subQ34,subQ33,subQ32,subQ31,subQ30,subQ29,subQ28,subQ27,subQ26,subQ25,subQ24,subQ23,subQ22,subQ21,subQ20,subQ19,subQ18,subQ17,subQ16,subQ15,subQ14,subQ13,subQ12,subQ11,subQ10,subQ9,subQ8,subQ7,subQ6,subQ5,subQ4,subQ3,subQ2,subQ1,subQ0,sQuery(id+"F0.wireOp",EDGE,"E20")])],"isStart":true})]}),makeQuery(id+"F10.opExtrude","SWEPT_FACE",FACE,{"disambiguationData":[OSD([sQuery(id+"F9.wireOp",EDGE,"E23.8.0")])]})]});}
            var Q1;
            {var subQ0=sQuery(id+"F0.wireOp",EDGE,"E18.14.2");var subQ1=sQuery(id+"F0.wireOp",EDGE,"E18.14.1");var subQ2=sQuery(id+"F0.wireOp",EDGE,"E18.14.0");var subQ3=sQuery(id+"F0.wireOp",EDGE,"E18.13.2");var subQ4=sQuery(id+"F0.wireOp",EDGE,"E18.13.1");var subQ5=sQuery(id+"F0.wireOp",EDGE,"E18.13.0");var subQ6=sQuery(id+"F0.wireOp",EDGE,"E18.12.2");var subQ7=sQuery(id+"F0.wireOp",EDGE,"E18.12.1");var subQ8=sQuery(id+"F0.wireOp",EDGE,"E18.12.0");var subQ9=sQuery(id+"F0.wireOp",EDGE,"E18.11.2");var subQ10=sQuery(id+"F0.wireOp",EDGE,"E18.11.1");var subQ11=sQuery(id+"F0.wireOp",EDGE,"E18.11.0");var subQ12=sQuery(id+"F0.wireOp",EDGE,"E18.10.2");var subQ13=sQuery(id+"F0.wireOp",EDGE,"E18.10.1");var subQ14=sQuery(id+"F0.wireOp",EDGE,"E18.10.0");var subQ15=sQuery(id+"F0.wireOp",EDGE,"E18.9.2");var subQ16=sQuery(id+"F0.wireOp",EDGE,"E18.9.1");var subQ17=sQuery(id+"F0.wireOp",EDGE,"E18.9.0");var subQ18=sQuery(id+"F0.wireOp",EDGE,"E18.8.2");var subQ19=sQuery(id+"F0.wireOp",EDGE,"E18.8.1");var subQ20=sQuery(id+"F0.wireOp",EDGE,"E18.8.0");var subQ21=sQuery(id+"F0.wireOp",EDGE,"E18.7.2");var subQ22=sQuery(id+"F0.wireOp",EDGE,"E18.7.1");var subQ23=sQuery(id+"F0.wireOp",EDGE,"E18.7.0");var subQ24=sQuery(id+"F0.wireOp",EDGE,"E18.6.2");var subQ25=sQuery(id+"F0.wireOp",EDGE,"E18.6.1");var subQ26=sQuery(id+"F0.wireOp",EDGE,"E18.6.0");var subQ27=sQuery(id+"F0.wireOp",EDGE,"E18.5.2");var subQ28=sQuery(id+"F0.wireOp",EDGE,"E18.5.1");var subQ29=sQuery(id+"F0.wireOp",EDGE,"E18.5.0");var subQ30=sQuery(id+"F0.wireOp",EDGE,"E18.4.2");var subQ31=sQuery(id+"F0.wireOp",EDGE,"E18.4.1");var subQ32=sQuery(id+"F0.wireOp",EDGE,"E18.4.0");var subQ33=sQuery(id+"F0.wireOp",EDGE,"E18.3.2");var subQ34=sQuery(id+"F0.wireOp",EDGE,"E18.3.1");var subQ35=sQuery(id+"F0.wireOp",EDGE,"E18.3.0");var subQ36=sQuery(id+"F0.wireOp",EDGE,"E18.2.2");var subQ37=sQuery(id+"F0.wireOp",EDGE,"E18.2.1");var subQ38=sQuery(id+"F0.wireOp",EDGE,"E18.2.0");var subQ39=sQuery(id+"F0.wireOp",EDGE,"E18.1.2");var subQ40=sQuery(id+"F0.wireOp",EDGE,"E18.1.1");var subQ41=sQuery(id+"F0.wireOp",EDGE,"E18.1.0");var subQ42=sQuery(id+"F0.wireOp",EDGE,"E14.MirrorC");var subQ43=sQuery(id+"F0.wireOp",EDGE,"E13");var subQ44=sQuery(id+"F0.wireOp",EDGE,"E12");var subQ45=sQuery(id+"F0.wireOp",EDGE,"E0");Q1=makeQuery(id+"F10.boolean.opBoolean","INTERSECT",EDGE,{"derivedFrom":[makeQuery(id+"F6.boolean.opBoolean","MERGE",FACE,{"derivedFrom":[makeQuery(id+"F1.opExtrude","CAP_FACE",FACE,{"disambiguationData":[OSD([subQ45,sQuery(id+"F0.wireOp",EDGE,"E9.5.0"),sQuery(id+"F0.wireOp",EDGE,"E9.5.1"),sQuery(id+"F0.wireOp",EDGE,"E1"),sQuery(id+"F0.wireOp",EDGE,"E9.5.3"),sQuery(id+"F0.wireOp",EDGE,"E9.5.4"),sQuery(id+"F0.wireOp",EDGE,"E8.trimOffspring"),sQuery(id+"F0.wireOp",EDGE,"E9.6.0"),sQuery(id+"F0.wireOp",EDGE,"E9.6.1"),sQuery(id+"F0.wireOp",EDGE,"E9.6.2"),sQuery(id+"F0.wireOp",EDGE,"E9.6.3"),sQuery(id+"F0.wireOp",EDGE,"E9.6.4"),sQuery(id+"F0.wireOp",EDGE,"E9.6.5"),sQuery(id+"F0.wireOp",EDGE,"E9.7.0"),sQuery(id+"F0.wireOp",EDGE,"E9.7.1"),sQuery(id+"F0.wireOp",EDGE,"E9.7.2"),sQuery(id+"F0.wireOp",EDGE,"E9.7.3"),sQuery(id+"F0.wireOp",EDGE,"E9.7.4"),sQuery(id+"F0.wireOp",EDGE,"E9.7.5"),sQuery(id+"F0.wireOp",EDGE,"E9.8.0"),sQuery(id+"F0.wireOp",EDGE,"E9.8.1"),sQuery(id+"F0.wireOp",EDGE,"E9.8.2"),sQuery(id+"F0.wireOp",EDGE,"E9.8.3"),sQuery(id+"F0.wireOp",EDGE,"E9.8.4"),sQuery(id+"F0.wireOp",EDGE,"E9.8.5"),sQuery(id+"F0.wireOp",EDGE,"E9.9.0"),sQuery(id+"F0.wireOp",EDGE,"E9.9.1"),sQuery(id+"F0.wireOp",EDGE,"E9.9.2"),sQuery(id+"F0.wireOp",EDGE,"E9.9.3"),sQuery(id+"F0.wireOp",EDGE,"E9.9.4"),sQuery(id+"F0.wireOp",EDGE,"E9.9.5"),subQ44,subQ43,subQ42,subQ41,subQ40,subQ39,subQ38,subQ37,subQ36,subQ35,subQ34,subQ33,subQ32,subQ31,subQ30,subQ29,subQ28,subQ27,subQ26,subQ25,subQ24,subQ23,subQ22,subQ21,subQ20,subQ19,subQ18,subQ17,subQ16,subQ15,subQ14,subQ13,subQ12,subQ11,subQ10,subQ9,subQ8,subQ7,subQ6,subQ5,subQ4,subQ3,subQ2,subQ1,subQ0,sQuery(id+"F0.wireOp",EDGE,"E19")])],"isStart":true}),makeQuery(id+"F6.opExtrude","CAP_FACE",FACE,{"disambiguationData":[OSD([subQ45,subQ44,subQ43,subQ42,subQ41,subQ40,subQ39,subQ38,subQ37,subQ36,subQ35,subQ34,subQ33,subQ32,subQ31,subQ30,subQ29,subQ28,subQ27,subQ26,subQ25,subQ24,subQ23,subQ22,subQ21,subQ20,subQ19,subQ18,subQ17,subQ16,subQ15,subQ14,subQ13,subQ12,subQ11,subQ10,subQ9,subQ8,subQ7,subQ6,subQ5,subQ4,subQ3,subQ2,subQ1,subQ0,sQuery(id+"F0.wireOp",EDGE,"E20")])],"isStart":true})]}),makeQuery(id+"F10.opExtrude","SWEPT_FACE",FACE,{"disambiguationData":[OSD([sQuery(id+"F9.wireOp",EDGE,"E23.9.0")])]})]});}
            var Q2;
            {var subQ0=sQuery(id+"F0.wireOp",EDGE,"E18.14.2");var subQ1=sQuery(id+"F0.wireOp",EDGE,"E18.14.1");var subQ2=sQuery(id+"F0.wireOp",EDGE,"E18.14.0");var subQ3=sQuery(id+"F0.wireOp",EDGE,"E18.13.2");var subQ4=sQuery(id+"F0.wireOp",EDGE,"E18.13.1");var subQ5=sQuery(id+"F0.wireOp",EDGE,"E18.13.0");var subQ6=sQuery(id+"F0.wireOp",EDGE,"E18.12.2");var subQ7=sQuery(id+"F0.wireOp",EDGE,"E18.12.1");var subQ8=sQuery(id+"F0.wireOp",EDGE,"E18.12.0");var subQ9=sQuery(id+"F0.wireOp",EDGE,"E18.11.2");var subQ10=sQuery(id+"F0.wireOp",EDGE,"E18.11.1");var subQ11=sQuery(id+"F0.wireOp",EDGE,"E18.11.0");var subQ12=sQuery(id+"F0.wireOp",EDGE,"E18.10.2");var subQ13=sQuery(id+"F0.wireOp",EDGE,"E18.10.1");var subQ14=sQuery(id+"F0.wireOp",EDGE,"E18.10.0");var subQ15=sQuery(id+"F0.wireOp",EDGE,"E18.9.2");var subQ16=sQuery(id+"F0.wireOp",EDGE,"E18.9.1");var subQ17=sQuery(id+"F0.wireOp",EDGE,"E18.9.0");var subQ18=sQuery(id+"F0.wireOp",EDGE,"E18.8.2");var subQ19=sQuery(id+"F0.wireOp",EDGE,"E18.8.1");var subQ20=sQuery(id+"F0.wireOp",EDGE,"E18.8.0");var subQ21=sQuery(id+"F0.wireOp",EDGE,"E18.7.2");var subQ22=sQuery(id+"F0.wireOp",EDGE,"E18.7.1");var subQ23=sQuery(id+"F0.wireOp",EDGE,"E18.7.0");var subQ24=sQuery(id+"F0.wireOp",EDGE,"E18.6.2");var subQ25=sQuery(id+"F0.wireOp",EDGE,"E18.6.1");var subQ26=sQuery(id+"F0.wireOp",EDGE,"E18.6.0");var subQ27=sQuery(id+"F0.wireOp",EDGE,"E18.5.2");var subQ28=sQuery(id+"F0.wireOp",EDGE,"E18.5.1");var subQ29=sQuery(id+"F0.wireOp",EDGE,"E18.5.0");var subQ30=sQuery(id+"F0.wireOp",EDGE,"E18.4.2");var subQ31=sQuery(id+"F0.wireOp",EDGE,"E18.4.1");var subQ32=sQuery(id+"F0.wireOp",EDGE,"E18.4.0");var subQ33=sQuery(id+"F0.wireOp",EDGE,"E18.3.2");var subQ34=sQuery(id+"F0.wireOp",EDGE,"E18.3.1");var subQ35=sQuery(id+"F0.wireOp",EDGE,"E18.3.0");var subQ36=sQuery(id+"F0.wireOp",EDGE,"E18.2.2");var subQ37=sQuery(id+"F0.wireOp",EDGE,"E18.2.1");var subQ38=sQuery(id+"F0.wireOp",EDGE,"E18.2.0");var subQ39=sQuery(id+"F0.wireOp",EDGE,"E18.1.2");var subQ40=sQuery(id+"F0.wireOp",EDGE,"E18.1.1");var subQ41=sQuery(id+"F0.wireOp",EDGE,"E18.1.0");var subQ42=sQuery(id+"F0.wireOp",EDGE,"E14.MirrorC");var subQ43=sQuery(id+"F0.wireOp",EDGE,"E13");var subQ44=sQuery(id+"F0.wireOp",EDGE,"E12");var subQ45=sQuery(id+"F0.wireOp",EDGE,"E0");Q2=makeQuery(id+"F10.boolean.opBoolean","INTERSECT",EDGE,{"derivedFrom":[makeQuery(id+"F6.boolean.opBoolean","MERGE",FACE,{"derivedFrom":[makeQuery(id+"F1.opExtrude","CAP_FACE",FACE,{"disambiguationData":[OSD([subQ45,sQuery(id+"F0.wireOp",EDGE,"E9.5.0"),sQuery(id+"F0.wireOp",EDGE,"E9.5.1"),sQuery(id+"F0.wireOp",EDGE,"E1"),sQuery(id+"F0.wireOp",EDGE,"E9.5.3"),sQuery(id+"F0.wireOp",EDGE,"E9.5.4"),sQuery(id+"F0.wireOp",EDGE,"E8.trimOffspring"),sQuery(id+"F0.wireOp",EDGE,"E9.6.0"),sQuery(id+"F0.wireOp",EDGE,"E9.6.1"),sQuery(id+"F0.wireOp",EDGE,"E9.6.2"),sQuery(id+"F0.wireOp",EDGE,"E9.6.3"),sQuery(id+"F0.wireOp",EDGE,"E9.6.4"),sQuery(id+"F0.wireOp",EDGE,"E9.6.5"),sQuery(id+"F0.wireOp",EDGE,"E9.7.0"),sQuery(id+"F0.wireOp",EDGE,"E9.7.1"),sQuery(id+"F0.wireOp",EDGE,"E9.7.2"),sQuery(id+"F0.wireOp",EDGE,"E9.7.3"),sQuery(id+"F0.wireOp",EDGE,"E9.7.4"),sQuery(id+"F0.wireOp",EDGE,"E9.7.5"),sQuery(id+"F0.wireOp",EDGE,"E9.8.0"),sQuery(id+"F0.wireOp",EDGE,"E9.8.1"),sQuery(id+"F0.wireOp",EDGE,"E9.8.2"),sQuery(id+"F0.wireOp",EDGE,"E9.8.3"),sQuery(id+"F0.wireOp",EDGE,"E9.8.4"),sQuery(id+"F0.wireOp",EDGE,"E9.8.5"),sQuery(id+"F0.wireOp",EDGE,"E9.9.0"),sQuery(id+"F0.wireOp",EDGE,"E9.9.1"),sQuery(id+"F0.wireOp",EDGE,"E9.9.2"),sQuery(id+"F0.wireOp",EDGE,"E9.9.3"),sQuery(id+"F0.wireOp",EDGE,"E9.9.4"),sQuery(id+"F0.wireOp",EDGE,"E9.9.5"),subQ44,subQ43,subQ42,subQ41,subQ40,subQ39,subQ38,subQ37,subQ36,subQ35,subQ34,subQ33,subQ32,subQ31,subQ30,subQ29,subQ28,subQ27,subQ26,subQ25,subQ24,subQ23,subQ22,subQ21,subQ20,subQ19,subQ18,subQ17,subQ16,subQ15,subQ14,subQ13,subQ12,subQ11,subQ10,subQ9,subQ8,subQ7,subQ6,subQ5,subQ4,subQ3,subQ2,subQ1,subQ0,sQuery(id+"F0.wireOp",EDGE,"E19")])],"isStart":true}),makeQuery(id+"F6.opExtrude","CAP_FACE",FACE,{"disambiguationData":[OSD([subQ45,subQ44,subQ43,subQ42,subQ41,subQ40,subQ39,subQ38,subQ37,subQ36,subQ35,subQ34,subQ33,subQ32,subQ31,subQ30,subQ29,subQ28,subQ27,subQ26,subQ25,subQ24,subQ23,subQ22,subQ21,subQ20,subQ19,subQ18,subQ17,subQ16,subQ15,subQ14,subQ13,subQ12,subQ11,subQ10,subQ9,subQ8,subQ7,subQ6,subQ5,subQ4,subQ3,subQ2,subQ1,subQ0,sQuery(id+"F0.wireOp",EDGE,"E20")])],"isStart":true})]}),makeQuery(id+"F10.opExtrude","SWEPT_FACE",FACE,{"disambiguationData":[OSD([sQuery(id+"F9.wireOp",EDGE,"E22")])]})]});}
            var Q3;
            {var subQ0=sQuery(id+"F0.wireOp",EDGE,"E20");Q3=makeQuery(id+"F10.boolean.opBoolean","INTERSECT",EDGE,{"derivedFrom":[makeQuery(id+"F6.boolean.opBoolean","SPLIT",FACE,{"disambiguationData":[TD([makeQuery(id+"F5.boolean.opBoolean","COPY",FACE,{"derivedFrom":makeQuery(id+"F5.opExtrude","SWEPT_FACE",FACE,{"disambiguationData":[OSD([sQuery(id+"F4.wireOp",EDGE,"E21")])]})})])],"derivedFrom":makeQuery(id+"F6.opExtrude","CAP_FACE",FACE,{"disambiguationData":[OSD([sQuery(id+"F0.wireOp",EDGE,"E0"),sQuery(id+"F0.wireOp",EDGE,"E12"),sQuery(id+"F0.wireOp",EDGE,"E13"),sQuery(id+"F0.wireOp",EDGE,"E14.MirrorC"),sQuery(id+"F0.wireOp",EDGE,"E18.1.0"),sQuery(id+"F0.wireOp",EDGE,"E18.1.1"),sQuery(id+"F0.wireOp",EDGE,"E18.1.2"),sQuery(id+"F0.wireOp",EDGE,"E18.2.0"),sQuery(id+"F0.wireOp",EDGE,"E18.2.1"),sQuery(id+"F0.wireOp",EDGE,"E18.2.2"),sQuery(id+"F0.wireOp",EDGE,"E18.3.0"),sQuery(id+"F0.wireOp",EDGE,"E18.3.1"),sQuery(id+"F0.wireOp",EDGE,"E18.3.2"),sQuery(id+"F0.wireOp",EDGE,"E18.4.0"),sQuery(id+"F0.wireOp",EDGE,"E18.4.1"),sQuery(id+"F0.wireOp",EDGE,"E18.4.2"),sQuery(id+"F0.wireOp",EDGE,"E18.5.0"),sQuery(id+"F0.wireOp",EDGE,"E18.5.1"),sQuery(id+"F0.wireOp",EDGE,"E18.5.2"),sQuery(id+"F0.wireOp",EDGE,"E18.6.0"),sQuery(id+"F0.wireOp",EDGE,"E18.6.1"),sQuery(id+"F0.wireOp",EDGE,"E18.6.2"),sQuery(id+"F0.wireOp",EDGE,"E18.7.0"),sQuery(id+"F0.wireOp",EDGE,"E18.7.1"),sQuery(id+"F0.wireOp",EDGE,"E18.7.2"),sQuery(id+"F0.wireOp",EDGE,"E18.8.0"),sQuery(id+"F0.wireOp",EDGE,"E18.8.1"),sQuery(id+"F0.wireOp",EDGE,"E18.8.2"),sQuery(id+"F0.wireOp",EDGE,"E18.9.0"),sQuery(id+"F0.wireOp",EDGE,"E18.9.1"),sQuery(id+"F0.wireOp",EDGE,"E18.9.2"),sQuery(id+"F0.wireOp",EDGE,"E18.10.0"),sQuery(id+"F0.wireOp",EDGE,"E18.10.1"),sQuery(id+"F0.wireOp",EDGE,"E18.10.2"),sQuery(id+"F0.wireOp",EDGE,"E18.11.0"),sQuery(id+"F0.wireOp",EDGE,"E18.11.1"),sQuery(id+"F0.wireOp",EDGE,"E18.11.2"),sQuery(id+"F0.wireOp",EDGE,"E18.12.0"),sQuery(id+"F0.wireOp",EDGE,"E18.12.1"),sQuery(id+"F0.wireOp",EDGE,"E18.12.2"),sQuery(id+"F0.wireOp",EDGE,"E18.13.0"),sQuery(id+"F0.wireOp",EDGE,"E18.13.1"),sQuery(id+"F0.wireOp",EDGE,"E18.13.2"),sQuery(id+"F0.wireOp",EDGE,"E18.14.0"),sQuery(id+"F0.wireOp",EDGE,"E18.14.1"),sQuery(id+"F0.wireOp",EDGE,"E18.14.2"),subQ0])],"isStart":false})}),makeQuery(id+"F10.opExtrude","SWEPT_FACE",FACE,{"disambiguationData":[OSD([sQuery(id+"F9.wireOp",EDGE,"E22")])]})]});}
            var Q4;
            {var subQ0=sQuery(id+"F0.wireOp",EDGE,"E20");Q4=makeQuery(id+"F10.boolean.opBoolean","INTERSECT",EDGE,{"derivedFrom":[makeQuery(id+"F6.boolean.opBoolean","SPLIT",FACE,{"disambiguationData":[TD([makeQuery(id+"F5.boolean.opBoolean","COPY",FACE,{"derivedFrom":makeQuery(id+"F5.opExtrude","SWEPT_FACE",FACE,{"disambiguationData":[OSD([sQuery(id+"F4.wireOp",EDGE,"E21")])]})})])],"derivedFrom":makeQuery(id+"F6.opExtrude","CAP_FACE",FACE,{"disambiguationData":[OSD([sQuery(id+"F0.wireOp",EDGE,"E0"),sQuery(id+"F0.wireOp",EDGE,"E12"),sQuery(id+"F0.wireOp",EDGE,"E13"),sQuery(id+"F0.wireOp",EDGE,"E14.MirrorC"),sQuery(id+"F0.wireOp",EDGE,"E18.1.0"),sQuery(id+"F0.wireOp",EDGE,"E18.1.1"),sQuery(id+"F0.wireOp",EDGE,"E18.1.2"),sQuery(id+"F0.wireOp",EDGE,"E18.2.0"),sQuery(id+"F0.wireOp",EDGE,"E18.2.1"),sQuery(id+"F0.wireOp",EDGE,"E18.2.2"),sQuery(id+"F0.wireOp",EDGE,"E18.3.0"),sQuery(id+"F0.wireOp",EDGE,"E18.3.1"),sQuery(id+"F0.wireOp",EDGE,"E18.3.2"),sQuery(id+"F0.wireOp",EDGE,"E18.4.0"),sQuery(id+"F0.wireOp",EDGE,"E18.4.1"),sQuery(id+"F0.wireOp",EDGE,"E18.4.2"),sQuery(id+"F0.wireOp",EDGE,"E18.5.0"),sQuery(id+"F0.wireOp",EDGE,"E18.5.1"),sQuery(id+"F0.wireOp",EDGE,"E18.5.2"),sQuery(id+"F0.wireOp",EDGE,"E18.6.0"),sQuery(id+"F0.wireOp",EDGE,"E18.6.1"),sQuery(id+"F0.wireOp",EDGE,"E18.6.2"),sQuery(id+"F0.wireOp",EDGE,"E18.7.0"),sQuery(id+"F0.wireOp",EDGE,"E18.7.1"),sQuery(id+"F0.wireOp",EDGE,"E18.7.2"),sQuery(id+"F0.wireOp",EDGE,"E18.8.0"),sQuery(id+"F0.wireOp",EDGE,"E18.8.1"),sQuery(id+"F0.wireOp",EDGE,"E18.8.2"),sQuery(id+"F0.wireOp",EDGE,"E18.9.0"),sQuery(id+"F0.wireOp",EDGE,"E18.9.1"),sQuery(id+"F0.wireOp",EDGE,"E18.9.2"),sQuery(id+"F0.wireOp",EDGE,"E18.10.0"),sQuery(id+"F0.wireOp",EDGE,"E18.10.1"),sQuery(id+"F0.wireOp",EDGE,"E18.10.2"),sQuery(id+"F0.wireOp",EDGE,"E18.11.0"),sQuery(id+"F0.wireOp",EDGE,"E18.11.1"),sQuery(id+"F0.wireOp",EDGE,"E18.11.2"),sQuery(id+"F0.wireOp",EDGE,"E18.12.0"),sQuery(id+"F0.wireOp",EDGE,"E18.12.1"),sQuery(id+"F0.wireOp",EDGE,"E18.12.2"),sQuery(id+"F0.wireOp",EDGE,"E18.13.0"),sQuery(id+"F0.wireOp",EDGE,"E18.13.1"),sQuery(id+"F0.wireOp",EDGE,"E18.13.2"),sQuery(id+"F0.wireOp",EDGE,"E18.14.0"),sQuery(id+"F0.wireOp",EDGE,"E18.14.1"),sQuery(id+"F0.wireOp",EDGE,"E18.14.2"),subQ0])],"isStart":false})}),makeQuery(id+"F10.opExtrude","SWEPT_FACE",FACE,{"disambiguationData":[OSD([sQuery(id+"F9.wireOp",EDGE,"E23.9.0")])]})]});}
            var Q5;
            {var subQ0=sQuery(id+"F0.wireOp",EDGE,"E20");Q5=makeQuery(id+"F10.boolean.opBoolean","INTERSECT",EDGE,{"derivedFrom":[makeQuery(id+"F6.boolean.opBoolean","SPLIT",FACE,{"disambiguationData":[TD([makeQuery(id+"F5.boolean.opBoolean","COPY",FACE,{"derivedFrom":makeQuery(id+"F5.opExtrude","SWEPT_FACE",FACE,{"disambiguationData":[OSD([sQuery(id+"F4.wireOp",EDGE,"E21")])]})})])],"derivedFrom":makeQuery(id+"F6.opExtrude","CAP_FACE",FACE,{"disambiguationData":[OSD([sQuery(id+"F0.wireOp",EDGE,"E0"),sQuery(id+"F0.wireOp",EDGE,"E12"),sQuery(id+"F0.wireOp",EDGE,"E13"),sQuery(id+"F0.wireOp",EDGE,"E14.MirrorC"),sQuery(id+"F0.wireOp",EDGE,"E18.1.0"),sQuery(id+"F0.wireOp",EDGE,"E18.1.1"),sQuery(id+"F0.wireOp",EDGE,"E18.1.2"),sQuery(id+"F0.wireOp",EDGE,"E18.2.0"),sQuery(id+"F0.wireOp",EDGE,"E18.2.1"),sQuery(id+"F0.wireOp",EDGE,"E18.2.2"),sQuery(id+"F0.wireOp",EDGE,"E18.3.0"),sQuery(id+"F0.wireOp",EDGE,"E18.3.1"),sQuery(id+"F0.wireOp",EDGE,"E18.3.2"),sQuery(id+"F0.wireOp",EDGE,"E18.4.0"),sQuery(id+"F0.wireOp",EDGE,"E18.4.1"),sQuery(id+"F0.wireOp",EDGE,"E18.4.2"),sQuery(id+"F0.wireOp",EDGE,"E18.5.0"),sQuery(id+"F0.wireOp",EDGE,"E18.5.1"),sQuery(id+"F0.wireOp",EDGE,"E18.5.2"),sQuery(id+"F0.wireOp",EDGE,"E18.6.0"),sQuery(id+"F0.wireOp",EDGE,"E18.6.1"),sQuery(id+"F0.wireOp",EDGE,"E18.6.2"),sQuery(id+"F0.wireOp",EDGE,"E18.7.0"),sQuery(id+"F0.wireOp",EDGE,"E18.7.1"),sQuery(id+"F0.wireOp",EDGE,"E18.7.2"),sQuery(id+"F0.wireOp",EDGE,"E18.8.0"),sQuery(id+"F0.wireOp",EDGE,"E18.8.1"),sQuery(id+"F0.wireOp",EDGE,"E18.8.2"),sQuery(id+"F0.wireOp",EDGE,"E18.9.0"),sQuery(id+"F0.wireOp",EDGE,"E18.9.1"),sQuery(id+"F0.wireOp",EDGE,"E18.9.2"),sQuery(id+"F0.wireOp",EDGE,"E18.10.0"),sQuery(id+"F0.wireOp",EDGE,"E18.10.1"),sQuery(id+"F0.wireOp",EDGE,"E18.10.2"),sQuery(id+"F0.wireOp",EDGE,"E18.11.0"),sQuery(id+"F0.wireOp",EDGE,"E18.11.1"),sQuery(id+"F0.wireOp",EDGE,"E18.11.2"),sQuery(id+"F0.wireOp",EDGE,"E18.12.0"),sQuery(id+"F0.wireOp",EDGE,"E18.12.1"),sQuery(id+"F0.wireOp",EDGE,"E18.12.2"),sQuery(id+"F0.wireOp",EDGE,"E18.13.0"),sQuery(id+"F0.wireOp",EDGE,"E18.13.1"),sQuery(id+"F0.wireOp",EDGE,"E18.13.2"),sQuery(id+"F0.wireOp",EDGE,"E18.14.0"),sQuery(id+"F0.wireOp",EDGE,"E18.14.1"),sQuery(id+"F0.wireOp",EDGE,"E18.14.2"),subQ0])],"isStart":false})}),makeQuery(id+"F10.opExtrude","SWEPT_FACE",FACE,{"disambiguationData":[OSD([sQuery(id+"F9.wireOp",EDGE,"E23.8.0")])]})]});}
            var Q6;
            {var subQ0=sQuery(id+"F0.wireOp",EDGE,"E18.14.2");var subQ1=sQuery(id+"F0.wireOp",EDGE,"E18.14.1");var subQ2=sQuery(id+"F0.wireOp",EDGE,"E18.14.0");var subQ3=sQuery(id+"F0.wireOp",EDGE,"E18.13.2");var subQ4=sQuery(id+"F0.wireOp",EDGE,"E18.13.1");var subQ5=sQuery(id+"F0.wireOp",EDGE,"E18.13.0");var subQ6=sQuery(id+"F0.wireOp",EDGE,"E18.12.2");var subQ7=sQuery(id+"F0.wireOp",EDGE,"E18.12.1");var subQ8=sQuery(id+"F0.wireOp",EDGE,"E18.12.0");var subQ9=sQuery(id+"F0.wireOp",EDGE,"E18.11.2");var subQ10=sQuery(id+"F0.wireOp",EDGE,"E18.11.1");var subQ11=sQuery(id+"F0.wireOp",EDGE,"E18.11.0");var subQ12=sQuery(id+"F0.wireOp",EDGE,"E18.10.2");var subQ13=sQuery(id+"F0.wireOp",EDGE,"E18.10.1");var subQ14=sQuery(id+"F0.wireOp",EDGE,"E18.10.0");var subQ15=sQuery(id+"F0.wireOp",EDGE,"E18.9.2");var subQ16=sQuery(id+"F0.wireOp",EDGE,"E18.9.1");var subQ17=sQuery(id+"F0.wireOp",EDGE,"E18.9.0");var subQ18=sQuery(id+"F0.wireOp",EDGE,"E18.8.2");var subQ19=sQuery(id+"F0.wireOp",EDGE,"E18.8.1");var subQ20=sQuery(id+"F0.wireOp",EDGE,"E18.8.0");var subQ21=sQuery(id+"F0.wireOp",EDGE,"E18.7.2");var subQ22=sQuery(id+"F0.wireOp",EDGE,"E18.7.1");var subQ23=sQuery(id+"F0.wireOp",EDGE,"E18.7.0");var subQ24=sQuery(id+"F0.wireOp",EDGE,"E18.6.2");var subQ25=sQuery(id+"F0.wireOp",EDGE,"E18.6.1");var subQ26=sQuery(id+"F0.wireOp",EDGE,"E18.6.0");var subQ27=sQuery(id+"F0.wireOp",EDGE,"E18.5.2");var subQ28=sQuery(id+"F0.wireOp",EDGE,"E18.5.1");var subQ29=sQuery(id+"F0.wireOp",EDGE,"E18.5.0");var subQ30=sQuery(id+"F0.wireOp",EDGE,"E18.4.2");var subQ31=sQuery(id+"F0.wireOp",EDGE,"E18.4.1");var subQ32=sQuery(id+"F0.wireOp",EDGE,"E18.4.0");var subQ33=sQuery(id+"F0.wireOp",EDGE,"E18.3.2");var subQ34=sQuery(id+"F0.wireOp",EDGE,"E18.3.1");var subQ35=sQuery(id+"F0.wireOp",EDGE,"E18.3.0");var subQ36=sQuery(id+"F0.wireOp",EDGE,"E18.2.2");var subQ37=sQuery(id+"F0.wireOp",EDGE,"E18.2.1");var subQ38=sQuery(id+"F0.wireOp",EDGE,"E18.2.0");var subQ39=sQuery(id+"F0.wireOp",EDGE,"E18.1.2");var subQ40=sQuery(id+"F0.wireOp",EDGE,"E18.1.1");var subQ41=sQuery(id+"F0.wireOp",EDGE,"E18.1.0");var subQ42=sQuery(id+"F0.wireOp",EDGE,"E14.MirrorC");var subQ43=sQuery(id+"F0.wireOp",EDGE,"E13");var subQ44=sQuery(id+"F0.wireOp",EDGE,"E12");var subQ45=sQuery(id+"F0.wireOp",EDGE,"E0");Q6=makeQuery(id+"F10.boolean.opBoolean","INTERSECT",EDGE,{"derivedFrom":[makeQuery(id+"F6.boolean.opBoolean","MERGE",FACE,{"derivedFrom":[makeQuery(id+"F1.opExtrude","CAP_FACE",FACE,{"disambiguationData":[OSD([subQ45,sQuery(id+"F0.wireOp",EDGE,"E9.5.0"),sQuery(id+"F0.wireOp",EDGE,"E9.5.1"),sQuery(id+"F0.wireOp",EDGE,"E1"),sQuery(id+"F0.wireOp",EDGE,"E9.5.3"),sQuery(id+"F0.wireOp",EDGE,"E9.5.4"),sQuery(id+"F0.wireOp",EDGE,"E8.trimOffspring"),sQuery(id+"F0.wireOp",EDGE,"E9.6.0"),sQuery(id+"F0.wireOp",EDGE,"E9.6.1"),sQuery(id+"F0.wireOp",EDGE,"E9.6.2"),sQuery(id+"F0.wireOp",EDGE,"E9.6.3"),sQuery(id+"F0.wireOp",EDGE,"E9.6.4"),sQuery(id+"F0.wireOp",EDGE,"E9.6.5"),sQuery(id+"F0.wireOp",EDGE,"E9.7.0"),sQuery(id+"F0.wireOp",EDGE,"E9.7.1"),sQuery(id+"F0.wireOp",EDGE,"E9.7.2"),sQuery(id+"F0.wireOp",EDGE,"E9.7.3"),sQuery(id+"F0.wireOp",EDGE,"E9.7.4"),sQuery(id+"F0.wireOp",EDGE,"E9.7.5"),sQuery(id+"F0.wireOp",EDGE,"E9.8.0"),sQuery(id+"F0.wireOp",EDGE,"E9.8.1"),sQuery(id+"F0.wireOp",EDGE,"E9.8.2"),sQuery(id+"F0.wireOp",EDGE,"E9.8.3"),sQuery(id+"F0.wireOp",EDGE,"E9.8.4"),sQuery(id+"F0.wireOp",EDGE,"E9.8.5"),sQuery(id+"F0.wireOp",EDGE,"E9.9.0"),sQuery(id+"F0.wireOp",EDGE,"E9.9.1"),sQuery(id+"F0.wireOp",EDGE,"E9.9.2"),sQuery(id+"F0.wireOp",EDGE,"E9.9.3"),sQuery(id+"F0.wireOp",EDGE,"E9.9.4"),sQuery(id+"F0.wireOp",EDGE,"E9.9.5"),subQ44,subQ43,subQ42,subQ41,subQ40,subQ39,subQ38,subQ37,subQ36,subQ35,subQ34,subQ33,subQ32,subQ31,subQ30,subQ29,subQ28,subQ27,subQ26,subQ25,subQ24,subQ23,subQ22,subQ21,subQ20,subQ19,subQ18,subQ17,subQ16,subQ15,subQ14,subQ13,subQ12,subQ11,subQ10,subQ9,subQ8,subQ7,subQ6,subQ5,subQ4,subQ3,subQ2,subQ1,subQ0,sQuery(id+"F0.wireOp",EDGE,"E19")])],"isStart":true}),makeQuery(id+"F6.opExtrude","CAP_FACE",FACE,{"disambiguationData":[OSD([subQ45,subQ44,subQ43,subQ42,subQ41,subQ40,subQ39,subQ38,subQ37,subQ36,subQ35,subQ34,subQ33,subQ32,subQ31,subQ30,subQ29,subQ28,subQ27,subQ26,subQ25,subQ24,subQ23,subQ22,subQ21,subQ20,subQ19,subQ18,subQ17,subQ16,subQ15,subQ14,subQ13,subQ12,subQ11,subQ10,subQ9,subQ8,subQ7,subQ6,subQ5,subQ4,subQ3,subQ2,subQ1,subQ0,sQuery(id+"F0.wireOp",EDGE,"E20")])],"isStart":true})]}),makeQuery(id+"F10.opExtrude","SWEPT_FACE",FACE,{"disambiguationData":[OSD([sQuery(id+"F9.wireOp",EDGE,"E23.7.0")])]})]});}
            var Q7;
            {var subQ0=sQuery(id+"F0.wireOp",EDGE,"E20");Q7=makeQuery(id+"F10.boolean.opBoolean","INTERSECT",EDGE,{"derivedFrom":[makeQuery(id+"F6.boolean.opBoolean","SPLIT",FACE,{"disambiguationData":[TD([makeQuery(id+"F5.boolean.opBoolean","COPY",FACE,{"derivedFrom":makeQuery(id+"F5.opExtrude","SWEPT_FACE",FACE,{"disambiguationData":[OSD([sQuery(id+"F4.wireOp",EDGE,"E21")])]})})])],"derivedFrom":makeQuery(id+"F6.opExtrude","CAP_FACE",FACE,{"disambiguationData":[OSD([sQuery(id+"F0.wireOp",EDGE,"E0"),sQuery(id+"F0.wireOp",EDGE,"E12"),sQuery(id+"F0.wireOp",EDGE,"E13"),sQuery(id+"F0.wireOp",EDGE,"E14.MirrorC"),sQuery(id+"F0.wireOp",EDGE,"E18.1.0"),sQuery(id+"F0.wireOp",EDGE,"E18.1.1"),sQuery(id+"F0.wireOp",EDGE,"E18.1.2"),sQuery(id+"F0.wireOp",EDGE,"E18.2.0"),sQuery(id+"F0.wireOp",EDGE,"E18.2.1"),sQuery(id+"F0.wireOp",EDGE,"E18.2.2"),sQuery(id+"F0.wireOp",EDGE,"E18.3.0"),sQuery(id+"F0.wireOp",EDGE,"E18.3.1"),sQuery(id+"F0.wireOp",EDGE,"E18.3.2"),sQuery(id+"F0.wireOp",EDGE,"E18.4.0"),sQuery(id+"F0.wireOp",EDGE,"E18.4.1"),sQuery(id+"F0.wireOp",EDGE,"E18.4.2"),sQuery(id+"F0.wireOp",EDGE,"E18.5.0"),sQuery(id+"F0.wireOp",EDGE,"E18.5.1"),sQuery(id+"F0.wireOp",EDGE,"E18.5.2"),sQuery(id+"F0.wireOp",EDGE,"E18.6.0"),sQuery(id+"F0.wireOp",EDGE,"E18.6.1"),sQuery(id+"F0.wireOp",EDGE,"E18.6.2"),sQuery(id+"F0.wireOp",EDGE,"E18.7.0"),sQuery(id+"F0.wireOp",EDGE,"E18.7.1"),sQuery(id+"F0.wireOp",EDGE,"E18.7.2"),sQuery(id+"F0.wireOp",EDGE,"E18.8.0"),sQuery(id+"F0.wireOp",EDGE,"E18.8.1"),sQuery(id+"F0.wireOp",EDGE,"E18.8.2"),sQuery(id+"F0.wireOp",EDGE,"E18.9.0"),sQuery(id+"F0.wireOp",EDGE,"E18.9.1"),sQuery(id+"F0.wireOp",EDGE,"E18.9.2"),sQuery(id+"F0.wireOp",EDGE,"E18.10.0"),sQuery(id+"F0.wireOp",EDGE,"E18.10.1"),sQuery(id+"F0.wireOp",EDGE,"E18.10.2"),sQuery(id+"F0.wireOp",EDGE,"E18.11.0"),sQuery(id+"F0.wireOp",EDGE,"E18.11.1"),sQuery(id+"F0.wireOp",EDGE,"E18.11.2"),sQuery(id+"F0.wireOp",EDGE,"E18.12.0"),sQuery(id+"F0.wireOp",EDGE,"E18.12.1"),sQuery(id+"F0.wireOp",EDGE,"E18.12.2"),sQuery(id+"F0.wireOp",EDGE,"E18.13.0"),sQuery(id+"F0.wireOp",EDGE,"E18.13.1"),sQuery(id+"F0.wireOp",EDGE,"E18.13.2"),sQuery(id+"F0.wireOp",EDGE,"E18.14.0"),sQuery(id+"F0.wireOp",EDGE,"E18.14.1"),sQuery(id+"F0.wireOp",EDGE,"E18.14.2"),subQ0])],"isStart":false})}),makeQuery(id+"F10.opExtrude","SWEPT_FACE",FACE,{"disambiguationData":[OSD([sQuery(id+"F9.wireOp",EDGE,"E23.7.0")])]})]});}
            var Q8;
            {var subQ0=sQuery(id+"F0.wireOp",EDGE,"E18.14.2");var subQ1=sQuery(id+"F0.wireOp",EDGE,"E18.14.1");var subQ2=sQuery(id+"F0.wireOp",EDGE,"E18.14.0");var subQ3=sQuery(id+"F0.wireOp",EDGE,"E18.13.2");var subQ4=sQuery(id+"F0.wireOp",EDGE,"E18.13.1");var subQ5=sQuery(id+"F0.wireOp",EDGE,"E18.13.0");var subQ6=sQuery(id+"F0.wireOp",EDGE,"E18.12.2");var subQ7=sQuery(id+"F0.wireOp",EDGE,"E18.12.1");var subQ8=sQuery(id+"F0.wireOp",EDGE,"E18.12.0");var subQ9=sQuery(id+"F0.wireOp",EDGE,"E18.11.2");var subQ10=sQuery(id+"F0.wireOp",EDGE,"E18.11.1");var subQ11=sQuery(id+"F0.wireOp",EDGE,"E18.11.0");var subQ12=sQuery(id+"F0.wireOp",EDGE,"E18.10.2");var subQ13=sQuery(id+"F0.wireOp",EDGE,"E18.10.1");var subQ14=sQuery(id+"F0.wireOp",EDGE,"E18.10.0");var subQ15=sQuery(id+"F0.wireOp",EDGE,"E18.9.2");var subQ16=sQuery(id+"F0.wireOp",EDGE,"E18.9.1");var subQ17=sQuery(id+"F0.wireOp",EDGE,"E18.9.0");var subQ18=sQuery(id+"F0.wireOp",EDGE,"E18.8.2");var subQ19=sQuery(id+"F0.wireOp",EDGE,"E18.8.1");var subQ20=sQuery(id+"F0.wireOp",EDGE,"E18.8.0");var subQ21=sQuery(id+"F0.wireOp",EDGE,"E18.7.2");var subQ22=sQuery(id+"F0.wireOp",EDGE,"E18.7.1");var subQ23=sQuery(id+"F0.wireOp",EDGE,"E18.7.0");var subQ24=sQuery(id+"F0.wireOp",EDGE,"E18.6.2");var subQ25=sQuery(id+"F0.wireOp",EDGE,"E18.6.1");var subQ26=sQuery(id+"F0.wireOp",EDGE,"E18.6.0");var subQ27=sQuery(id+"F0.wireOp",EDGE,"E18.5.2");var subQ28=sQuery(id+"F0.wireOp",EDGE,"E18.5.1");var subQ29=sQuery(id+"F0.wireOp",EDGE,"E18.5.0");var subQ30=sQuery(id+"F0.wireOp",EDGE,"E18.4.2");var subQ31=sQuery(id+"F0.wireOp",EDGE,"E18.4.1");var subQ32=sQuery(id+"F0.wireOp",EDGE,"E18.4.0");var subQ33=sQuery(id+"F0.wireOp",EDGE,"E18.3.2");var subQ34=sQuery(id+"F0.wireOp",EDGE,"E18.3.1");var subQ35=sQuery(id+"F0.wireOp",EDGE,"E18.3.0");var subQ36=sQuery(id+"F0.wireOp",EDGE,"E18.2.2");var subQ37=sQuery(id+"F0.wireOp",EDGE,"E18.2.1");var subQ38=sQuery(id+"F0.wireOp",EDGE,"E18.2.0");var subQ39=sQuery(id+"F0.wireOp",EDGE,"E18.1.2");var subQ40=sQuery(id+"F0.wireOp",EDGE,"E18.1.1");var subQ41=sQuery(id+"F0.wireOp",EDGE,"E18.1.0");var subQ42=sQuery(id+"F0.wireOp",EDGE,"E14.MirrorC");var subQ43=sQuery(id+"F0.wireOp",EDGE,"E13");var subQ44=sQuery(id+"F0.wireOp",EDGE,"E12");var subQ45=sQuery(id+"F0.wireOp",EDGE,"E0");Q8=makeQuery(id+"F10.boolean.opBoolean","INTERSECT",EDGE,{"derivedFrom":[makeQuery(id+"F6.boolean.opBoolean","MERGE",FACE,{"derivedFrom":[makeQuery(id+"F1.opExtrude","CAP_FACE",FACE,{"disambiguationData":[OSD([subQ45,sQuery(id+"F0.wireOp",EDGE,"E9.5.0"),sQuery(id+"F0.wireOp",EDGE,"E9.5.1"),sQuery(id+"F0.wireOp",EDGE,"E1"),sQuery(id+"F0.wireOp",EDGE,"E9.5.3"),sQuery(id+"F0.wireOp",EDGE,"E9.5.4"),sQuery(id+"F0.wireOp",EDGE,"E8.trimOffspring"),sQuery(id+"F0.wireOp",EDGE,"E9.6.0"),sQuery(id+"F0.wireOp",EDGE,"E9.6.1"),sQuery(id+"F0.wireOp",EDGE,"E9.6.2"),sQuery(id+"F0.wireOp",EDGE,"E9.6.3"),sQuery(id+"F0.wireOp",EDGE,"E9.6.4"),sQuery(id+"F0.wireOp",EDGE,"E9.6.5"),sQuery(id+"F0.wireOp",EDGE,"E9.7.0"),sQuery(id+"F0.wireOp",EDGE,"E9.7.1"),sQuery(id+"F0.wireOp",EDGE,"E9.7.2"),sQuery(id+"F0.wireOp",EDGE,"E9.7.3"),sQuery(id+"F0.wireOp",EDGE,"E9.7.4"),sQuery(id+"F0.wireOp",EDGE,"E9.7.5"),sQuery(id+"F0.wireOp",EDGE,"E9.8.0"),sQuery(id+"F0.wireOp",EDGE,"E9.8.1"),sQuery(id+"F0.wireOp",EDGE,"E9.8.2"),sQuery(id+"F0.wireOp",EDGE,"E9.8.3"),sQuery(id+"F0.wireOp",EDGE,"E9.8.4"),sQuery(id+"F0.wireOp",EDGE,"E9.8.5"),sQuery(id+"F0.wireOp",EDGE,"E9.9.0"),sQuery(id+"F0.wireOp",EDGE,"E9.9.1"),sQuery(id+"F0.wireOp",EDGE,"E9.9.2"),sQuery(id+"F0.wireOp",EDGE,"E9.9.3"),sQuery(id+"F0.wireOp",EDGE,"E9.9.4"),sQuery(id+"F0.wireOp",EDGE,"E9.9.5"),subQ44,subQ43,subQ42,subQ41,subQ40,subQ39,subQ38,subQ37,subQ36,subQ35,subQ34,subQ33,subQ32,subQ31,subQ30,subQ29,subQ28,subQ27,subQ26,subQ25,subQ24,subQ23,subQ22,subQ21,subQ20,subQ19,subQ18,subQ17,subQ16,subQ15,subQ14,subQ13,subQ12,subQ11,subQ10,subQ9,subQ8,subQ7,subQ6,subQ5,subQ4,subQ3,subQ2,subQ1,subQ0,sQuery(id+"F0.wireOp",EDGE,"E19")])],"isStart":true}),makeQuery(id+"F6.opExtrude","CAP_FACE",FACE,{"disambiguationData":[OSD([subQ45,subQ44,subQ43,subQ42,subQ41,subQ40,subQ39,subQ38,subQ37,subQ36,subQ35,subQ34,subQ33,subQ32,subQ31,subQ30,subQ29,subQ28,subQ27,subQ26,subQ25,subQ24,subQ23,subQ22,subQ21,subQ20,subQ19,subQ18,subQ17,subQ16,subQ15,subQ14,subQ13,subQ12,subQ11,subQ10,subQ9,subQ8,subQ7,subQ6,subQ5,subQ4,subQ3,subQ2,subQ1,subQ0,sQuery(id+"F0.wireOp",EDGE,"E20")])],"isStart":true})]}),makeQuery(id+"F10.opExtrude","SWEPT_FACE",FACE,{"disambiguationData":[OSD([sQuery(id+"F9.wireOp",EDGE,"E23.6.0")])]})]});}
            var Q9;
            {var subQ0=sQuery(id+"F0.wireOp",EDGE,"E20");Q9=makeQuery(id+"F10.boolean.opBoolean","INTERSECT",EDGE,{"derivedFrom":[makeQuery(id+"F6.boolean.opBoolean","SPLIT",FACE,{"disambiguationData":[TD([makeQuery(id+"F5.boolean.opBoolean","COPY",FACE,{"derivedFrom":makeQuery(id+"F5.opExtrude","SWEPT_FACE",FACE,{"disambiguationData":[OSD([sQuery(id+"F4.wireOp",EDGE,"E21")])]})})])],"derivedFrom":makeQuery(id+"F6.opExtrude","CAP_FACE",FACE,{"disambiguationData":[OSD([sQuery(id+"F0.wireOp",EDGE,"E0"),sQuery(id+"F0.wireOp",EDGE,"E12"),sQuery(id+"F0.wireOp",EDGE,"E13"),sQuery(id+"F0.wireOp",EDGE,"E14.MirrorC"),sQuery(id+"F0.wireOp",EDGE,"E18.1.0"),sQuery(id+"F0.wireOp",EDGE,"E18.1.1"),sQuery(id+"F0.wireOp",EDGE,"E18.1.2"),sQuery(id+"F0.wireOp",EDGE,"E18.2.0"),sQuery(id+"F0.wireOp",EDGE,"E18.2.1"),sQuery(id+"F0.wireOp",EDGE,"E18.2.2"),sQuery(id+"F0.wireOp",EDGE,"E18.3.0"),sQuery(id+"F0.wireOp",EDGE,"E18.3.1"),sQuery(id+"F0.wireOp",EDGE,"E18.3.2"),sQuery(id+"F0.wireOp",EDGE,"E18.4.0"),sQuery(id+"F0.wireOp",EDGE,"E18.4.1"),sQuery(id+"F0.wireOp",EDGE,"E18.4.2"),sQuery(id+"F0.wireOp",EDGE,"E18.5.0"),sQuery(id+"F0.wireOp",EDGE,"E18.5.1"),sQuery(id+"F0.wireOp",EDGE,"E18.5.2"),sQuery(id+"F0.wireOp",EDGE,"E18.6.0"),sQuery(id+"F0.wireOp",EDGE,"E18.6.1"),sQuery(id+"F0.wireOp",EDGE,"E18.6.2"),sQuery(id+"F0.wireOp",EDGE,"E18.7.0"),sQuery(id+"F0.wireOp",EDGE,"E18.7.1"),sQuery(id+"F0.wireOp",EDGE,"E18.7.2"),sQuery(id+"F0.wireOp",EDGE,"E18.8.0"),sQuery(id+"F0.wireOp",EDGE,"E18.8.1"),sQuery(id+"F0.wireOp",EDGE,"E18.8.2"),sQuery(id+"F0.wireOp",EDGE,"E18.9.0"),sQuery(id+"F0.wireOp",EDGE,"E18.9.1"),sQuery(id+"F0.wireOp",EDGE,"E18.9.2"),sQuery(id+"F0.wireOp",EDGE,"E18.10.0"),sQuery(id+"F0.wireOp",EDGE,"E18.10.1"),sQuery(id+"F0.wireOp",EDGE,"E18.10.2"),sQuery(id+"F0.wireOp",EDGE,"E18.11.0"),sQuery(id+"F0.wireOp",EDGE,"E18.11.1"),sQuery(id+"F0.wireOp",EDGE,"E18.11.2"),sQuery(id+"F0.wireOp",EDGE,"E18.12.0"),sQuery(id+"F0.wireOp",EDGE,"E18.12.1"),sQuery(id+"F0.wireOp",EDGE,"E18.12.2"),sQuery(id+"F0.wireOp",EDGE,"E18.13.0"),sQuery(id+"F0.wireOp",EDGE,"E18.13.1"),sQuery(id+"F0.wireOp",EDGE,"E18.13.2"),sQuery(id+"F0.wireOp",EDGE,"E18.14.0"),sQuery(id+"F0.wireOp",EDGE,"E18.14.1"),sQuery(id+"F0.wireOp",EDGE,"E18.14.2"),subQ0])],"isStart":false})}),makeQuery(id+"F10.opExtrude","SWEPT_FACE",FACE,{"disambiguationData":[OSD([sQuery(id+"F9.wireOp",EDGE,"E23.6.0")])]})]});}
            var Q10;
            {var subQ0=sQuery(id+"F0.wireOp",EDGE,"E18.14.2");var subQ1=sQuery(id+"F0.wireOp",EDGE,"E18.14.1");var subQ2=sQuery(id+"F0.wireOp",EDGE,"E18.14.0");var subQ3=sQuery(id+"F0.wireOp",EDGE,"E18.13.2");var subQ4=sQuery(id+"F0.wireOp",EDGE,"E18.13.1");var subQ5=sQuery(id+"F0.wireOp",EDGE,"E18.13.0");var subQ6=sQuery(id+"F0.wireOp",EDGE,"E18.12.2");var subQ7=sQuery(id+"F0.wireOp",EDGE,"E18.12.1");var subQ8=sQuery(id+"F0.wireOp",EDGE,"E18.12.0");var subQ9=sQuery(id+"F0.wireOp",EDGE,"E18.11.2");var subQ10=sQuery(id+"F0.wireOp",EDGE,"E18.11.1");var subQ11=sQuery(id+"F0.wireOp",EDGE,"E18.11.0");var subQ12=sQuery(id+"F0.wireOp",EDGE,"E18.10.2");var subQ13=sQuery(id+"F0.wireOp",EDGE,"E18.10.1");var subQ14=sQuery(id+"F0.wireOp",EDGE,"E18.10.0");var subQ15=sQuery(id+"F0.wireOp",EDGE,"E18.9.2");var subQ16=sQuery(id+"F0.wireOp",EDGE,"E18.9.1");var subQ17=sQuery(id+"F0.wireOp",EDGE,"E18.9.0");var subQ18=sQuery(id+"F0.wireOp",EDGE,"E18.8.2");var subQ19=sQuery(id+"F0.wireOp",EDGE,"E18.8.1");var subQ20=sQuery(id+"F0.wireOp",EDGE,"E18.8.0");var subQ21=sQuery(id+"F0.wireOp",EDGE,"E18.7.2");var subQ22=sQuery(id+"F0.wireOp",EDGE,"E18.7.1");var subQ23=sQuery(id+"F0.wireOp",EDGE,"E18.7.0");var subQ24=sQuery(id+"F0.wireOp",EDGE,"E18.6.2");var subQ25=sQuery(id+"F0.wireOp",EDGE,"E18.6.1");var subQ26=sQuery(id+"F0.wireOp",EDGE,"E18.6.0");var subQ27=sQuery(id+"F0.wireOp",EDGE,"E18.5.2");var subQ28=sQuery(id+"F0.wireOp",EDGE,"E18.5.1");var subQ29=sQuery(id+"F0.wireOp",EDGE,"E18.5.0");var subQ30=sQuery(id+"F0.wireOp",EDGE,"E18.4.2");var subQ31=sQuery(id+"F0.wireOp",EDGE,"E18.4.1");var subQ32=sQuery(id+"F0.wireOp",EDGE,"E18.4.0");var subQ33=sQuery(id+"F0.wireOp",EDGE,"E18.3.2");var subQ34=sQuery(id+"F0.wireOp",EDGE,"E18.3.1");var subQ35=sQuery(id+"F0.wireOp",EDGE,"E18.3.0");var subQ36=sQuery(id+"F0.wireOp",EDGE,"E18.2.2");var subQ37=sQuery(id+"F0.wireOp",EDGE,"E18.2.1");var subQ38=sQuery(id+"F0.wireOp",EDGE,"E18.2.0");var subQ39=sQuery(id+"F0.wireOp",EDGE,"E18.1.2");var subQ40=sQuery(id+"F0.wireOp",EDGE,"E18.1.1");var subQ41=sQuery(id+"F0.wireOp",EDGE,"E18.1.0");var subQ42=sQuery(id+"F0.wireOp",EDGE,"E14.MirrorC");var subQ43=sQuery(id+"F0.wireOp",EDGE,"E13");var subQ44=sQuery(id+"F0.wireOp",EDGE,"E12");var subQ45=sQuery(id+"F0.wireOp",EDGE,"E0");Q10=makeQuery(id+"F10.boolean.opBoolean","INTERSECT",EDGE,{"derivedFrom":[makeQuery(id+"F6.boolean.opBoolean","MERGE",FACE,{"derivedFrom":[makeQuery(id+"F1.opExtrude","CAP_FACE",FACE,{"disambiguationData":[OSD([subQ45,sQuery(id+"F0.wireOp",EDGE,"E9.5.0"),sQuery(id+"F0.wireOp",EDGE,"E9.5.1"),sQuery(id+"F0.wireOp",EDGE,"E1"),sQuery(id+"F0.wireOp",EDGE,"E9.5.3"),sQuery(id+"F0.wireOp",EDGE,"E9.5.4"),sQuery(id+"F0.wireOp",EDGE,"E8.trimOffspring"),sQuery(id+"F0.wireOp",EDGE,"E9.6.0"),sQuery(id+"F0.wireOp",EDGE,"E9.6.1"),sQuery(id+"F0.wireOp",EDGE,"E9.6.2"),sQuery(id+"F0.wireOp",EDGE,"E9.6.3"),sQuery(id+"F0.wireOp",EDGE,"E9.6.4"),sQuery(id+"F0.wireOp",EDGE,"E9.6.5"),sQuery(id+"F0.wireOp",EDGE,"E9.7.0"),sQuery(id+"F0.wireOp",EDGE,"E9.7.1"),sQuery(id+"F0.wireOp",EDGE,"E9.7.2"),sQuery(id+"F0.wireOp",EDGE,"E9.7.3"),sQuery(id+"F0.wireOp",EDGE,"E9.7.4"),sQuery(id+"F0.wireOp",EDGE,"E9.7.5"),sQuery(id+"F0.wireOp",EDGE,"E9.8.0"),sQuery(id+"F0.wireOp",EDGE,"E9.8.1"),sQuery(id+"F0.wireOp",EDGE,"E9.8.2"),sQuery(id+"F0.wireOp",EDGE,"E9.8.3"),sQuery(id+"F0.wireOp",EDGE,"E9.8.4"),sQuery(id+"F0.wireOp",EDGE,"E9.8.5"),sQuery(id+"F0.wireOp",EDGE,"E9.9.0"),sQuery(id+"F0.wireOp",EDGE,"E9.9.1"),sQuery(id+"F0.wireOp",EDGE,"E9.9.2"),sQuery(id+"F0.wireOp",EDGE,"E9.9.3"),sQuery(id+"F0.wireOp",EDGE,"E9.9.4"),sQuery(id+"F0.wireOp",EDGE,"E9.9.5"),subQ44,subQ43,subQ42,subQ41,subQ40,subQ39,subQ38,subQ37,subQ36,subQ35,subQ34,subQ33,subQ32,subQ31,subQ30,subQ29,subQ28,subQ27,subQ26,subQ25,subQ24,subQ23,subQ22,subQ21,subQ20,subQ19,subQ18,subQ17,subQ16,subQ15,subQ14,subQ13,subQ12,subQ11,subQ10,subQ9,subQ8,subQ7,subQ6,subQ5,subQ4,subQ3,subQ2,subQ1,subQ0,sQuery(id+"F0.wireOp",EDGE,"E19")])],"isStart":true}),makeQuery(id+"F6.opExtrude","CAP_FACE",FACE,{"disambiguationData":[OSD([subQ45,subQ44,subQ43,subQ42,subQ41,subQ40,subQ39,subQ38,subQ37,subQ36,subQ35,subQ34,subQ33,subQ32,subQ31,subQ30,subQ29,subQ28,subQ27,subQ26,subQ25,subQ24,subQ23,subQ22,subQ21,subQ20,subQ19,subQ18,subQ17,subQ16,subQ15,subQ14,subQ13,subQ12,subQ11,subQ10,subQ9,subQ8,subQ7,subQ6,subQ5,subQ4,subQ3,subQ2,subQ1,subQ0,sQuery(id+"F0.wireOp",EDGE,"E20")])],"isStart":true})]}),makeQuery(id+"F10.opExtrude","SWEPT_FACE",FACE,{"disambiguationData":[OSD([sQuery(id+"F9.wireOp",EDGE,"E23.5.0")])]})]});}
            var Q11;
            {var subQ0=sQuery(id+"F0.wireOp",EDGE,"E20");Q11=makeQuery(id+"F10.boolean.opBoolean","INTERSECT",EDGE,{"derivedFrom":[makeQuery(id+"F6.boolean.opBoolean","SPLIT",FACE,{"disambiguationData":[TD([makeQuery(id+"F5.boolean.opBoolean","COPY",FACE,{"derivedFrom":makeQuery(id+"F5.opExtrude","SWEPT_FACE",FACE,{"disambiguationData":[OSD([sQuery(id+"F4.wireOp",EDGE,"E21")])]})})])],"derivedFrom":makeQuery(id+"F6.opExtrude","CAP_FACE",FACE,{"disambiguationData":[OSD([sQuery(id+"F0.wireOp",EDGE,"E0"),sQuery(id+"F0.wireOp",EDGE,"E12"),sQuery(id+"F0.wireOp",EDGE,"E13"),sQuery(id+"F0.wireOp",EDGE,"E14.MirrorC"),sQuery(id+"F0.wireOp",EDGE,"E18.1.0"),sQuery(id+"F0.wireOp",EDGE,"E18.1.1"),sQuery(id+"F0.wireOp",EDGE,"E18.1.2"),sQuery(id+"F0.wireOp",EDGE,"E18.2.0"),sQuery(id+"F0.wireOp",EDGE,"E18.2.1"),sQuery(id+"F0.wireOp",EDGE,"E18.2.2"),sQuery(id+"F0.wireOp",EDGE,"E18.3.0"),sQuery(id+"F0.wireOp",EDGE,"E18.3.1"),sQuery(id+"F0.wireOp",EDGE,"E18.3.2"),sQuery(id+"F0.wireOp",EDGE,"E18.4.0"),sQuery(id+"F0.wireOp",EDGE,"E18.4.1"),sQuery(id+"F0.wireOp",EDGE,"E18.4.2"),sQuery(id+"F0.wireOp",EDGE,"E18.5.0"),sQuery(id+"F0.wireOp",EDGE,"E18.5.1"),sQuery(id+"F0.wireOp",EDGE,"E18.5.2"),sQuery(id+"F0.wireOp",EDGE,"E18.6.0"),sQuery(id+"F0.wireOp",EDGE,"E18.6.1"),sQuery(id+"F0.wireOp",EDGE,"E18.6.2"),sQuery(id+"F0.wireOp",EDGE,"E18.7.0"),sQuery(id+"F0.wireOp",EDGE,"E18.7.1"),sQuery(id+"F0.wireOp",EDGE,"E18.7.2"),sQuery(id+"F0.wireOp",EDGE,"E18.8.0"),sQuery(id+"F0.wireOp",EDGE,"E18.8.1"),sQuery(id+"F0.wireOp",EDGE,"E18.8.2"),sQuery(id+"F0.wireOp",EDGE,"E18.9.0"),sQuery(id+"F0.wireOp",EDGE,"E18.9.1"),sQuery(id+"F0.wireOp",EDGE,"E18.9.2"),sQuery(id+"F0.wireOp",EDGE,"E18.10.0"),sQuery(id+"F0.wireOp",EDGE,"E18.10.1"),sQuery(id+"F0.wireOp",EDGE,"E18.10.2"),sQuery(id+"F0.wireOp",EDGE,"E18.11.0"),sQuery(id+"F0.wireOp",EDGE,"E18.11.1"),sQuery(id+"F0.wireOp",EDGE,"E18.11.2"),sQuery(id+"F0.wireOp",EDGE,"E18.12.0"),sQuery(id+"F0.wireOp",EDGE,"E18.12.1"),sQuery(id+"F0.wireOp",EDGE,"E18.12.2"),sQuery(id+"F0.wireOp",EDGE,"E18.13.0"),sQuery(id+"F0.wireOp",EDGE,"E18.13.1"),sQuery(id+"F0.wireOp",EDGE,"E18.13.2"),sQuery(id+"F0.wireOp",EDGE,"E18.14.0"),sQuery(id+"F0.wireOp",EDGE,"E18.14.1"),sQuery(id+"F0.wireOp",EDGE,"E18.14.2"),subQ0])],"isStart":false})}),makeQuery(id+"F10.opExtrude","SWEPT_FACE",FACE,{"disambiguationData":[OSD([sQuery(id+"F9.wireOp",EDGE,"E23.5.0")])]})]});}
            var Q12;
            {var subQ0=sQuery(id+"F0.wireOp",EDGE,"E18.14.2");var subQ1=sQuery(id+"F0.wireOp",EDGE,"E18.14.1");var subQ2=sQuery(id+"F0.wireOp",EDGE,"E18.14.0");var subQ3=sQuery(id+"F0.wireOp",EDGE,"E18.13.2");var subQ4=sQuery(id+"F0.wireOp",EDGE,"E18.13.1");var subQ5=sQuery(id+"F0.wireOp",EDGE,"E18.13.0");var subQ6=sQuery(id+"F0.wireOp",EDGE,"E18.12.2");var subQ7=sQuery(id+"F0.wireOp",EDGE,"E18.12.1");var subQ8=sQuery(id+"F0.wireOp",EDGE,"E18.12.0");var subQ9=sQuery(id+"F0.wireOp",EDGE,"E18.11.2");var subQ10=sQuery(id+"F0.wireOp",EDGE,"E18.11.1");var subQ11=sQuery(id+"F0.wireOp",EDGE,"E18.11.0");var subQ12=sQuery(id+"F0.wireOp",EDGE,"E18.10.2");var subQ13=sQuery(id+"F0.wireOp",EDGE,"E18.10.1");var subQ14=sQuery(id+"F0.wireOp",EDGE,"E18.10.0");var subQ15=sQuery(id+"F0.wireOp",EDGE,"E18.9.2");var subQ16=sQuery(id+"F0.wireOp",EDGE,"E18.9.1");var subQ17=sQuery(id+"F0.wireOp",EDGE,"E18.9.0");var subQ18=sQuery(id+"F0.wireOp",EDGE,"E18.8.2");var subQ19=sQuery(id+"F0.wireOp",EDGE,"E18.8.1");var subQ20=sQuery(id+"F0.wireOp",EDGE,"E18.8.0");var subQ21=sQuery(id+"F0.wireOp",EDGE,"E18.7.2");var subQ22=sQuery(id+"F0.wireOp",EDGE,"E18.7.1");var subQ23=sQuery(id+"F0.wireOp",EDGE,"E18.7.0");var subQ24=sQuery(id+"F0.wireOp",EDGE,"E18.6.2");var subQ25=sQuery(id+"F0.wireOp",EDGE,"E18.6.1");var subQ26=sQuery(id+"F0.wireOp",EDGE,"E18.6.0");var subQ27=sQuery(id+"F0.wireOp",EDGE,"E18.5.2");var subQ28=sQuery(id+"F0.wireOp",EDGE,"E18.5.1");var subQ29=sQuery(id+"F0.wireOp",EDGE,"E18.5.0");var subQ30=sQuery(id+"F0.wireOp",EDGE,"E18.4.2");var subQ31=sQuery(id+"F0.wireOp",EDGE,"E18.4.1");var subQ32=sQuery(id+"F0.wireOp",EDGE,"E18.4.0");var subQ33=sQuery(id+"F0.wireOp",EDGE,"E18.3.2");var subQ34=sQuery(id+"F0.wireOp",EDGE,"E18.3.1");var subQ35=sQuery(id+"F0.wireOp",EDGE,"E18.3.0");var subQ36=sQuery(id+"F0.wireOp",EDGE,"E18.2.2");var subQ37=sQuery(id+"F0.wireOp",EDGE,"E18.2.1");var subQ38=sQuery(id+"F0.wireOp",EDGE,"E18.2.0");var subQ39=sQuery(id+"F0.wireOp",EDGE,"E18.1.2");var subQ40=sQuery(id+"F0.wireOp",EDGE,"E18.1.1");var subQ41=sQuery(id+"F0.wireOp",EDGE,"E18.1.0");var subQ42=sQuery(id+"F0.wireOp",EDGE,"E14.MirrorC");var subQ43=sQuery(id+"F0.wireOp",EDGE,"E13");var subQ44=sQuery(id+"F0.wireOp",EDGE,"E12");var subQ45=sQuery(id+"F0.wireOp",EDGE,"E0");Q12=makeQuery(id+"F10.boolean.opBoolean","INTERSECT",EDGE,{"derivedFrom":[makeQuery(id+"F6.boolean.opBoolean","MERGE",FACE,{"derivedFrom":[makeQuery(id+"F1.opExtrude","CAP_FACE",FACE,{"disambiguationData":[OSD([subQ45,sQuery(id+"F0.wireOp",EDGE,"E9.5.0"),sQuery(id+"F0.wireOp",EDGE,"E9.5.1"),sQuery(id+"F0.wireOp",EDGE,"E1"),sQuery(id+"F0.wireOp",EDGE,"E9.5.3"),sQuery(id+"F0.wireOp",EDGE,"E9.5.4"),sQuery(id+"F0.wireOp",EDGE,"E8.trimOffspring"),sQuery(id+"F0.wireOp",EDGE,"E9.6.0"),sQuery(id+"F0.wireOp",EDGE,"E9.6.1"),sQuery(id+"F0.wireOp",EDGE,"E9.6.2"),sQuery(id+"F0.wireOp",EDGE,"E9.6.3"),sQuery(id+"F0.wireOp",EDGE,"E9.6.4"),sQuery(id+"F0.wireOp",EDGE,"E9.6.5"),sQuery(id+"F0.wireOp",EDGE,"E9.7.0"),sQuery(id+"F0.wireOp",EDGE,"E9.7.1"),sQuery(id+"F0.wireOp",EDGE,"E9.7.2"),sQuery(id+"F0.wireOp",EDGE,"E9.7.3"),sQuery(id+"F0.wireOp",EDGE,"E9.7.4"),sQuery(id+"F0.wireOp",EDGE,"E9.7.5"),sQuery(id+"F0.wireOp",EDGE,"E9.8.0"),sQuery(id+"F0.wireOp",EDGE,"E9.8.1"),sQuery(id+"F0.wireOp",EDGE,"E9.8.2"),sQuery(id+"F0.wireOp",EDGE,"E9.8.3"),sQuery(id+"F0.wireOp",EDGE,"E9.8.4"),sQuery(id+"F0.wireOp",EDGE,"E9.8.5"),sQuery(id+"F0.wireOp",EDGE,"E9.9.0"),sQuery(id+"F0.wireOp",EDGE,"E9.9.1"),sQuery(id+"F0.wireOp",EDGE,"E9.9.2"),sQuery(id+"F0.wireOp",EDGE,"E9.9.3"),sQuery(id+"F0.wireOp",EDGE,"E9.9.4"),sQuery(id+"F0.wireOp",EDGE,"E9.9.5"),subQ44,subQ43,subQ42,subQ41,subQ40,subQ39,subQ38,subQ37,subQ36,subQ35,subQ34,subQ33,subQ32,subQ31,subQ30,subQ29,subQ28,subQ27,subQ26,subQ25,subQ24,subQ23,subQ22,subQ21,subQ20,subQ19,subQ18,subQ17,subQ16,subQ15,subQ14,subQ13,subQ12,subQ11,subQ10,subQ9,subQ8,subQ7,subQ6,subQ5,subQ4,subQ3,subQ2,subQ1,subQ0,sQuery(id+"F0.wireOp",EDGE,"E19")])],"isStart":true}),makeQuery(id+"F6.opExtrude","CAP_FACE",FACE,{"disambiguationData":[OSD([subQ45,subQ44,subQ43,subQ42,subQ41,subQ40,subQ39,subQ38,subQ37,subQ36,subQ35,subQ34,subQ33,subQ32,subQ31,subQ30,subQ29,subQ28,subQ27,subQ26,subQ25,subQ24,subQ23,subQ22,subQ21,subQ20,subQ19,subQ18,subQ17,subQ16,subQ15,subQ14,subQ13,subQ12,subQ11,subQ10,subQ9,subQ8,subQ7,subQ6,subQ5,subQ4,subQ3,subQ2,subQ1,subQ0,sQuery(id+"F0.wireOp",EDGE,"E20")])],"isStart":true})]}),makeQuery(id+"F10.opExtrude","SWEPT_FACE",FACE,{"disambiguationData":[OSD([sQuery(id+"F9.wireOp",EDGE,"E23.4.0")])]})]});}
            var Q13;
            {var subQ0=sQuery(id+"F0.wireOp",EDGE,"E20");Q13=makeQuery(id+"F10.boolean.opBoolean","INTERSECT",EDGE,{"derivedFrom":[makeQuery(id+"F6.boolean.opBoolean","SPLIT",FACE,{"disambiguationData":[TD([makeQuery(id+"F5.boolean.opBoolean","COPY",FACE,{"derivedFrom":makeQuery(id+"F5.opExtrude","SWEPT_FACE",FACE,{"disambiguationData":[OSD([sQuery(id+"F4.wireOp",EDGE,"E21")])]})})])],"derivedFrom":makeQuery(id+"F6.opExtrude","CAP_FACE",FACE,{"disambiguationData":[OSD([sQuery(id+"F0.wireOp",EDGE,"E0"),sQuery(id+"F0.wireOp",EDGE,"E12"),sQuery(id+"F0.wireOp",EDGE,"E13"),sQuery(id+"F0.wireOp",EDGE,"E14.MirrorC"),sQuery(id+"F0.wireOp",EDGE,"E18.1.0"),sQuery(id+"F0.wireOp",EDGE,"E18.1.1"),sQuery(id+"F0.wireOp",EDGE,"E18.1.2"),sQuery(id+"F0.wireOp",EDGE,"E18.2.0"),sQuery(id+"F0.wireOp",EDGE,"E18.2.1"),sQuery(id+"F0.wireOp",EDGE,"E18.2.2"),sQuery(id+"F0.wireOp",EDGE,"E18.3.0"),sQuery(id+"F0.wireOp",EDGE,"E18.3.1"),sQuery(id+"F0.wireOp",EDGE,"E18.3.2"),sQuery(id+"F0.wireOp",EDGE,"E18.4.0"),sQuery(id+"F0.wireOp",EDGE,"E18.4.1"),sQuery(id+"F0.wireOp",EDGE,"E18.4.2"),sQuery(id+"F0.wireOp",EDGE,"E18.5.0"),sQuery(id+"F0.wireOp",EDGE,"E18.5.1"),sQuery(id+"F0.wireOp",EDGE,"E18.5.2"),sQuery(id+"F0.wireOp",EDGE,"E18.6.0"),sQuery(id+"F0.wireOp",EDGE,"E18.6.1"),sQuery(id+"F0.wireOp",EDGE,"E18.6.2"),sQuery(id+"F0.wireOp",EDGE,"E18.7.0"),sQuery(id+"F0.wireOp",EDGE,"E18.7.1"),sQuery(id+"F0.wireOp",EDGE,"E18.7.2"),sQuery(id+"F0.wireOp",EDGE,"E18.8.0"),sQuery(id+"F0.wireOp",EDGE,"E18.8.1"),sQuery(id+"F0.wireOp",EDGE,"E18.8.2"),sQuery(id+"F0.wireOp",EDGE,"E18.9.0"),sQuery(id+"F0.wireOp",EDGE,"E18.9.1"),sQuery(id+"F0.wireOp",EDGE,"E18.9.2"),sQuery(id+"F0.wireOp",EDGE,"E18.10.0"),sQuery(id+"F0.wireOp",EDGE,"E18.10.1"),sQuery(id+"F0.wireOp",EDGE,"E18.10.2"),sQuery(id+"F0.wireOp",EDGE,"E18.11.0"),sQuery(id+"F0.wireOp",EDGE,"E18.11.1"),sQuery(id+"F0.wireOp",EDGE,"E18.11.2"),sQuery(id+"F0.wireOp",EDGE,"E18.12.0"),sQuery(id+"F0.wireOp",EDGE,"E18.12.1"),sQuery(id+"F0.wireOp",EDGE,"E18.12.2"),sQuery(id+"F0.wireOp",EDGE,"E18.13.0"),sQuery(id+"F0.wireOp",EDGE,"E18.13.1"),sQuery(id+"F0.wireOp",EDGE,"E18.13.2"),sQuery(id+"F0.wireOp",EDGE,"E18.14.0"),sQuery(id+"F0.wireOp",EDGE,"E18.14.1"),sQuery(id+"F0.wireOp",EDGE,"E18.14.2"),subQ0])],"isStart":false})}),makeQuery(id+"F10.opExtrude","SWEPT_FACE",FACE,{"disambiguationData":[OSD([sQuery(id+"F9.wireOp",EDGE,"E23.4.0")])]})]});}
            var Q14;
            {var subQ0=sQuery(id+"F0.wireOp",EDGE,"E18.14.2");var subQ1=sQuery(id+"F0.wireOp",EDGE,"E18.14.1");var subQ2=sQuery(id+"F0.wireOp",EDGE,"E18.14.0");var subQ3=sQuery(id+"F0.wireOp",EDGE,"E18.13.2");var subQ4=sQuery(id+"F0.wireOp",EDGE,"E18.13.1");var subQ5=sQuery(id+"F0.wireOp",EDGE,"E18.13.0");var subQ6=sQuery(id+"F0.wireOp",EDGE,"E18.12.2");var subQ7=sQuery(id+"F0.wireOp",EDGE,"E18.12.1");var subQ8=sQuery(id+"F0.wireOp",EDGE,"E18.12.0");var subQ9=sQuery(id+"F0.wireOp",EDGE,"E18.11.2");var subQ10=sQuery(id+"F0.wireOp",EDGE,"E18.11.1");var subQ11=sQuery(id+"F0.wireOp",EDGE,"E18.11.0");var subQ12=sQuery(id+"F0.wireOp",EDGE,"E18.10.2");var subQ13=sQuery(id+"F0.wireOp",EDGE,"E18.10.1");var subQ14=sQuery(id+"F0.wireOp",EDGE,"E18.10.0");var subQ15=sQuery(id+"F0.wireOp",EDGE,"E18.9.2");var subQ16=sQuery(id+"F0.wireOp",EDGE,"E18.9.1");var subQ17=sQuery(id+"F0.wireOp",EDGE,"E18.9.0");var subQ18=sQuery(id+"F0.wireOp",EDGE,"E18.8.2");var subQ19=sQuery(id+"F0.wireOp",EDGE,"E18.8.1");var subQ20=sQuery(id+"F0.wireOp",EDGE,"E18.8.0");var subQ21=sQuery(id+"F0.wireOp",EDGE,"E18.7.2");var subQ22=sQuery(id+"F0.wireOp",EDGE,"E18.7.1");var subQ23=sQuery(id+"F0.wireOp",EDGE,"E18.7.0");var subQ24=sQuery(id+"F0.wireOp",EDGE,"E18.6.2");var subQ25=sQuery(id+"F0.wireOp",EDGE,"E18.6.1");var subQ26=sQuery(id+"F0.wireOp",EDGE,"E18.6.0");var subQ27=sQuery(id+"F0.wireOp",EDGE,"E18.5.2");var subQ28=sQuery(id+"F0.wireOp",EDGE,"E18.5.1");var subQ29=sQuery(id+"F0.wireOp",EDGE,"E18.5.0");var subQ30=sQuery(id+"F0.wireOp",EDGE,"E18.4.2");var subQ31=sQuery(id+"F0.wireOp",EDGE,"E18.4.1");var subQ32=sQuery(id+"F0.wireOp",EDGE,"E18.4.0");var subQ33=sQuery(id+"F0.wireOp",EDGE,"E18.3.2");var subQ34=sQuery(id+"F0.wireOp",EDGE,"E18.3.1");var subQ35=sQuery(id+"F0.wireOp",EDGE,"E18.3.0");var subQ36=sQuery(id+"F0.wireOp",EDGE,"E18.2.2");var subQ37=sQuery(id+"F0.wireOp",EDGE,"E18.2.1");var subQ38=sQuery(id+"F0.wireOp",EDGE,"E18.2.0");var subQ39=sQuery(id+"F0.wireOp",EDGE,"E18.1.2");var subQ40=sQuery(id+"F0.wireOp",EDGE,"E18.1.1");var subQ41=sQuery(id+"F0.wireOp",EDGE,"E18.1.0");var subQ42=sQuery(id+"F0.wireOp",EDGE,"E14.MirrorC");var subQ43=sQuery(id+"F0.wireOp",EDGE,"E13");var subQ44=sQuery(id+"F0.wireOp",EDGE,"E12");var subQ45=sQuery(id+"F0.wireOp",EDGE,"E0");Q14=makeQuery(id+"F10.boolean.opBoolean","INTERSECT",EDGE,{"derivedFrom":[makeQuery(id+"F6.boolean.opBoolean","MERGE",FACE,{"derivedFrom":[makeQuery(id+"F1.opExtrude","CAP_FACE",FACE,{"disambiguationData":[OSD([subQ45,sQuery(id+"F0.wireOp",EDGE,"E9.5.0"),sQuery(id+"F0.wireOp",EDGE,"E9.5.1"),sQuery(id+"F0.wireOp",EDGE,"E1"),sQuery(id+"F0.wireOp",EDGE,"E9.5.3"),sQuery(id+"F0.wireOp",EDGE,"E9.5.4"),sQuery(id+"F0.wireOp",EDGE,"E8.trimOffspring"),sQuery(id+"F0.wireOp",EDGE,"E9.6.0"),sQuery(id+"F0.wireOp",EDGE,"E9.6.1"),sQuery(id+"F0.wireOp",EDGE,"E9.6.2"),sQuery(id+"F0.wireOp",EDGE,"E9.6.3"),sQuery(id+"F0.wireOp",EDGE,"E9.6.4"),sQuery(id+"F0.wireOp",EDGE,"E9.6.5"),sQuery(id+"F0.wireOp",EDGE,"E9.7.0"),sQuery(id+"F0.wireOp",EDGE,"E9.7.1"),sQuery(id+"F0.wireOp",EDGE,"E9.7.2"),sQuery(id+"F0.wireOp",EDGE,"E9.7.3"),sQuery(id+"F0.wireOp",EDGE,"E9.7.4"),sQuery(id+"F0.wireOp",EDGE,"E9.7.5"),sQuery(id+"F0.wireOp",EDGE,"E9.8.0"),sQuery(id+"F0.wireOp",EDGE,"E9.8.1"),sQuery(id+"F0.wireOp",EDGE,"E9.8.2"),sQuery(id+"F0.wireOp",EDGE,"E9.8.3"),sQuery(id+"F0.wireOp",EDGE,"E9.8.4"),sQuery(id+"F0.wireOp",EDGE,"E9.8.5"),sQuery(id+"F0.wireOp",EDGE,"E9.9.0"),sQuery(id+"F0.wireOp",EDGE,"E9.9.1"),sQuery(id+"F0.wireOp",EDGE,"E9.9.2"),sQuery(id+"F0.wireOp",EDGE,"E9.9.3"),sQuery(id+"F0.wireOp",EDGE,"E9.9.4"),sQuery(id+"F0.wireOp",EDGE,"E9.9.5"),subQ44,subQ43,subQ42,subQ41,subQ40,subQ39,subQ38,subQ37,subQ36,subQ35,subQ34,subQ33,subQ32,subQ31,subQ30,subQ29,subQ28,subQ27,subQ26,subQ25,subQ24,subQ23,subQ22,subQ21,subQ20,subQ19,subQ18,subQ17,subQ16,subQ15,subQ14,subQ13,subQ12,subQ11,subQ10,subQ9,subQ8,subQ7,subQ6,subQ5,subQ4,subQ3,subQ2,subQ1,subQ0,sQuery(id+"F0.wireOp",EDGE,"E19")])],"isStart":true}),makeQuery(id+"F6.opExtrude","CAP_FACE",FACE,{"disambiguationData":[OSD([subQ45,subQ44,subQ43,subQ42,subQ41,subQ40,subQ39,subQ38,subQ37,subQ36,subQ35,subQ34,subQ33,subQ32,subQ31,subQ30,subQ29,subQ28,subQ27,subQ26,subQ25,subQ24,subQ23,subQ22,subQ21,subQ20,subQ19,subQ18,subQ17,subQ16,subQ15,subQ14,subQ13,subQ12,subQ11,subQ10,subQ9,subQ8,subQ7,subQ6,subQ5,subQ4,subQ3,subQ2,subQ1,subQ0,sQuery(id+"F0.wireOp",EDGE,"E20")])],"isStart":true})]}),makeQuery(id+"F10.opExtrude","SWEPT_FACE",FACE,{"disambiguationData":[OSD([sQuery(id+"F9.wireOp",EDGE,"E23.3.0")])]})]});}
            var Q15;
            {var subQ0=sQuery(id+"F0.wireOp",EDGE,"E20");Q15=makeQuery(id+"F10.boolean.opBoolean","INTERSECT",EDGE,{"derivedFrom":[makeQuery(id+"F6.boolean.opBoolean","SPLIT",FACE,{"disambiguationData":[TD([makeQuery(id+"F5.boolean.opBoolean","COPY",FACE,{"derivedFrom":makeQuery(id+"F5.opExtrude","SWEPT_FACE",FACE,{"disambiguationData":[OSD([sQuery(id+"F4.wireOp",EDGE,"E21")])]})})])],"derivedFrom":makeQuery(id+"F6.opExtrude","CAP_FACE",FACE,{"disambiguationData":[OSD([sQuery(id+"F0.wireOp",EDGE,"E0"),sQuery(id+"F0.wireOp",EDGE,"E12"),sQuery(id+"F0.wireOp",EDGE,"E13"),sQuery(id+"F0.wireOp",EDGE,"E14.MirrorC"),sQuery(id+"F0.wireOp",EDGE,"E18.1.0"),sQuery(id+"F0.wireOp",EDGE,"E18.1.1"),sQuery(id+"F0.wireOp",EDGE,"E18.1.2"),sQuery(id+"F0.wireOp",EDGE,"E18.2.0"),sQuery(id+"F0.wireOp",EDGE,"E18.2.1"),sQuery(id+"F0.wireOp",EDGE,"E18.2.2"),sQuery(id+"F0.wireOp",EDGE,"E18.3.0"),sQuery(id+"F0.wireOp",EDGE,"E18.3.1"),sQuery(id+"F0.wireOp",EDGE,"E18.3.2"),sQuery(id+"F0.wireOp",EDGE,"E18.4.0"),sQuery(id+"F0.wireOp",EDGE,"E18.4.1"),sQuery(id+"F0.wireOp",EDGE,"E18.4.2"),sQuery(id+"F0.wireOp",EDGE,"E18.5.0"),sQuery(id+"F0.wireOp",EDGE,"E18.5.1"),sQuery(id+"F0.wireOp",EDGE,"E18.5.2"),sQuery(id+"F0.wireOp",EDGE,"E18.6.0"),sQuery(id+"F0.wireOp",EDGE,"E18.6.1"),sQuery(id+"F0.wireOp",EDGE,"E18.6.2"),sQuery(id+"F0.wireOp",EDGE,"E18.7.0"),sQuery(id+"F0.wireOp",EDGE,"E18.7.1"),sQuery(id+"F0.wireOp",EDGE,"E18.7.2"),sQuery(id+"F0.wireOp",EDGE,"E18.8.0"),sQuery(id+"F0.wireOp",EDGE,"E18.8.1"),sQuery(id+"F0.wireOp",EDGE,"E18.8.2"),sQuery(id+"F0.wireOp",EDGE,"E18.9.0"),sQuery(id+"F0.wireOp",EDGE,"E18.9.1"),sQuery(id+"F0.wireOp",EDGE,"E18.9.2"),sQuery(id+"F0.wireOp",EDGE,"E18.10.0"),sQuery(id+"F0.wireOp",EDGE,"E18.10.1"),sQuery(id+"F0.wireOp",EDGE,"E18.10.2"),sQuery(id+"F0.wireOp",EDGE,"E18.11.0"),sQuery(id+"F0.wireOp",EDGE,"E18.11.1"),sQuery(id+"F0.wireOp",EDGE,"E18.11.2"),sQuery(id+"F0.wireOp",EDGE,"E18.12.0"),sQuery(id+"F0.wireOp",EDGE,"E18.12.1"),sQuery(id+"F0.wireOp",EDGE,"E18.12.2"),sQuery(id+"F0.wireOp",EDGE,"E18.13.0"),sQuery(id+"F0.wireOp",EDGE,"E18.13.1"),sQuery(id+"F0.wireOp",EDGE,"E18.13.2"),sQuery(id+"F0.wireOp",EDGE,"E18.14.0"),sQuery(id+"F0.wireOp",EDGE,"E18.14.1"),sQuery(id+"F0.wireOp",EDGE,"E18.14.2"),subQ0])],"isStart":false})}),makeQuery(id+"F10.opExtrude","SWEPT_FACE",FACE,{"disambiguationData":[OSD([sQuery(id+"F9.wireOp",EDGE,"E23.3.0")])]})]});}
            var Q16;
            {var subQ0=sQuery(id+"F0.wireOp",EDGE,"E18.14.2");var subQ1=sQuery(id+"F0.wireOp",EDGE,"E18.14.1");var subQ2=sQuery(id+"F0.wireOp",EDGE,"E18.14.0");var subQ3=sQuery(id+"F0.wireOp",EDGE,"E18.13.2");var subQ4=sQuery(id+"F0.wireOp",EDGE,"E18.13.1");var subQ5=sQuery(id+"F0.wireOp",EDGE,"E18.13.0");var subQ6=sQuery(id+"F0.wireOp",EDGE,"E18.12.2");var subQ7=sQuery(id+"F0.wireOp",EDGE,"E18.12.1");var subQ8=sQuery(id+"F0.wireOp",EDGE,"E18.12.0");var subQ9=sQuery(id+"F0.wireOp",EDGE,"E18.11.2");var subQ10=sQuery(id+"F0.wireOp",EDGE,"E18.11.1");var subQ11=sQuery(id+"F0.wireOp",EDGE,"E18.11.0");var subQ12=sQuery(id+"F0.wireOp",EDGE,"E18.10.2");var subQ13=sQuery(id+"F0.wireOp",EDGE,"E18.10.1");var subQ14=sQuery(id+"F0.wireOp",EDGE,"E18.10.0");var subQ15=sQuery(id+"F0.wireOp",EDGE,"E18.9.2");var subQ16=sQuery(id+"F0.wireOp",EDGE,"E18.9.1");var subQ17=sQuery(id+"F0.wireOp",EDGE,"E18.9.0");var subQ18=sQuery(id+"F0.wireOp",EDGE,"E18.8.2");var subQ19=sQuery(id+"F0.wireOp",EDGE,"E18.8.1");var subQ20=sQuery(id+"F0.wireOp",EDGE,"E18.8.0");var subQ21=sQuery(id+"F0.wireOp",EDGE,"E18.7.2");var subQ22=sQuery(id+"F0.wireOp",EDGE,"E18.7.1");var subQ23=sQuery(id+"F0.wireOp",EDGE,"E18.7.0");var subQ24=sQuery(id+"F0.wireOp",EDGE,"E18.6.2");var subQ25=sQuery(id+"F0.wireOp",EDGE,"E18.6.1");var subQ26=sQuery(id+"F0.wireOp",EDGE,"E18.6.0");var subQ27=sQuery(id+"F0.wireOp",EDGE,"E18.5.2");var subQ28=sQuery(id+"F0.wireOp",EDGE,"E18.5.1");var subQ29=sQuery(id+"F0.wireOp",EDGE,"E18.5.0");var subQ30=sQuery(id+"F0.wireOp",EDGE,"E18.4.2");var subQ31=sQuery(id+"F0.wireOp",EDGE,"E18.4.1");var subQ32=sQuery(id+"F0.wireOp",EDGE,"E18.4.0");var subQ33=sQuery(id+"F0.wireOp",EDGE,"E18.3.2");var subQ34=sQuery(id+"F0.wireOp",EDGE,"E18.3.1");var subQ35=sQuery(id+"F0.wireOp",EDGE,"E18.3.0");var subQ36=sQuery(id+"F0.wireOp",EDGE,"E18.2.2");var subQ37=sQuery(id+"F0.wireOp",EDGE,"E18.2.1");var subQ38=sQuery(id+"F0.wireOp",EDGE,"E18.2.0");var subQ39=sQuery(id+"F0.wireOp",EDGE,"E18.1.2");var subQ40=sQuery(id+"F0.wireOp",EDGE,"E18.1.1");var subQ41=sQuery(id+"F0.wireOp",EDGE,"E18.1.0");var subQ42=sQuery(id+"F0.wireOp",EDGE,"E14.MirrorC");var subQ43=sQuery(id+"F0.wireOp",EDGE,"E13");var subQ44=sQuery(id+"F0.wireOp",EDGE,"E12");var subQ45=sQuery(id+"F0.wireOp",EDGE,"E0");Q16=makeQuery(id+"F10.boolean.opBoolean","INTERSECT",EDGE,{"derivedFrom":[makeQuery(id+"F6.boolean.opBoolean","MERGE",FACE,{"derivedFrom":[makeQuery(id+"F1.opExtrude","CAP_FACE",FACE,{"disambiguationData":[OSD([subQ45,sQuery(id+"F0.wireOp",EDGE,"E9.5.0"),sQuery(id+"F0.wireOp",EDGE,"E9.5.1"),sQuery(id+"F0.wireOp",EDGE,"E1"),sQuery(id+"F0.wireOp",EDGE,"E9.5.3"),sQuery(id+"F0.wireOp",EDGE,"E9.5.4"),sQuery(id+"F0.wireOp",EDGE,"E8.trimOffspring"),sQuery(id+"F0.wireOp",EDGE,"E9.6.0"),sQuery(id+"F0.wireOp",EDGE,"E9.6.1"),sQuery(id+"F0.wireOp",EDGE,"E9.6.2"),sQuery(id+"F0.wireOp",EDGE,"E9.6.3"),sQuery(id+"F0.wireOp",EDGE,"E9.6.4"),sQuery(id+"F0.wireOp",EDGE,"E9.6.5"),sQuery(id+"F0.wireOp",EDGE,"E9.7.0"),sQuery(id+"F0.wireOp",EDGE,"E9.7.1"),sQuery(id+"F0.wireOp",EDGE,"E9.7.2"),sQuery(id+"F0.wireOp",EDGE,"E9.7.3"),sQuery(id+"F0.wireOp",EDGE,"E9.7.4"),sQuery(id+"F0.wireOp",EDGE,"E9.7.5"),sQuery(id+"F0.wireOp",EDGE,"E9.8.0"),sQuery(id+"F0.wireOp",EDGE,"E9.8.1"),sQuery(id+"F0.wireOp",EDGE,"E9.8.2"),sQuery(id+"F0.wireOp",EDGE,"E9.8.3"),sQuery(id+"F0.wireOp",EDGE,"E9.8.4"),sQuery(id+"F0.wireOp",EDGE,"E9.8.5"),sQuery(id+"F0.wireOp",EDGE,"E9.9.0"),sQuery(id+"F0.wireOp",EDGE,"E9.9.1"),sQuery(id+"F0.wireOp",EDGE,"E9.9.2"),sQuery(id+"F0.wireOp",EDGE,"E9.9.3"),sQuery(id+"F0.wireOp",EDGE,"E9.9.4"),sQuery(id+"F0.wireOp",EDGE,"E9.9.5"),subQ44,subQ43,subQ42,subQ41,subQ40,subQ39,subQ38,subQ37,subQ36,subQ35,subQ34,subQ33,subQ32,subQ31,subQ30,subQ29,subQ28,subQ27,subQ26,subQ25,subQ24,subQ23,subQ22,subQ21,subQ20,subQ19,subQ18,subQ17,subQ16,subQ15,subQ14,subQ13,subQ12,subQ11,subQ10,subQ9,subQ8,subQ7,subQ6,subQ5,subQ4,subQ3,subQ2,subQ1,subQ0,sQuery(id+"F0.wireOp",EDGE,"E19")])],"isStart":true}),makeQuery(id+"F6.opExtrude","CAP_FACE",FACE,{"disambiguationData":[OSD([subQ45,subQ44,subQ43,subQ42,subQ41,subQ40,subQ39,subQ38,subQ37,subQ36,subQ35,subQ34,subQ33,subQ32,subQ31,subQ30,subQ29,subQ28,subQ27,subQ26,subQ25,subQ24,subQ23,subQ22,subQ21,subQ20,subQ19,subQ18,subQ17,subQ16,subQ15,subQ14,subQ13,subQ12,subQ11,subQ10,subQ9,subQ8,subQ7,subQ6,subQ5,subQ4,subQ3,subQ2,subQ1,subQ0,sQuery(id+"F0.wireOp",EDGE,"E20")])],"isStart":true})]}),makeQuery(id+"F10.opExtrude","SWEPT_FACE",FACE,{"disambiguationData":[OSD([sQuery(id+"F9.wireOp",EDGE,"E23.2.0")])]})]});}
            var Q17;
            {var subQ0=sQuery(id+"F0.wireOp",EDGE,"E20");Q17=makeQuery(id+"F10.boolean.opBoolean","INTERSECT",EDGE,{"derivedFrom":[makeQuery(id+"F6.boolean.opBoolean","SPLIT",FACE,{"disambiguationData":[TD([makeQuery(id+"F5.boolean.opBoolean","COPY",FACE,{"derivedFrom":makeQuery(id+"F5.opExtrude","SWEPT_FACE",FACE,{"disambiguationData":[OSD([sQuery(id+"F4.wireOp",EDGE,"E21")])]})})])],"derivedFrom":makeQuery(id+"F6.opExtrude","CAP_FACE",FACE,{"disambiguationData":[OSD([sQuery(id+"F0.wireOp",EDGE,"E0"),sQuery(id+"F0.wireOp",EDGE,"E12"),sQuery(id+"F0.wireOp",EDGE,"E13"),sQuery(id+"F0.wireOp",EDGE,"E14.MirrorC"),sQuery(id+"F0.wireOp",EDGE,"E18.1.0"),sQuery(id+"F0.wireOp",EDGE,"E18.1.1"),sQuery(id+"F0.wireOp",EDGE,"E18.1.2"),sQuery(id+"F0.wireOp",EDGE,"E18.2.0"),sQuery(id+"F0.wireOp",EDGE,"E18.2.1"),sQuery(id+"F0.wireOp",EDGE,"E18.2.2"),sQuery(id+"F0.wireOp",EDGE,"E18.3.0"),sQuery(id+"F0.wireOp",EDGE,"E18.3.1"),sQuery(id+"F0.wireOp",EDGE,"E18.3.2"),sQuery(id+"F0.wireOp",EDGE,"E18.4.0"),sQuery(id+"F0.wireOp",EDGE,"E18.4.1"),sQuery(id+"F0.wireOp",EDGE,"E18.4.2"),sQuery(id+"F0.wireOp",EDGE,"E18.5.0"),sQuery(id+"F0.wireOp",EDGE,"E18.5.1"),sQuery(id+"F0.wireOp",EDGE,"E18.5.2"),sQuery(id+"F0.wireOp",EDGE,"E18.6.0"),sQuery(id+"F0.wireOp",EDGE,"E18.6.1"),sQuery(id+"F0.wireOp",EDGE,"E18.6.2"),sQuery(id+"F0.wireOp",EDGE,"E18.7.0"),sQuery(id+"F0.wireOp",EDGE,"E18.7.1"),sQuery(id+"F0.wireOp",EDGE,"E18.7.2"),sQuery(id+"F0.wireOp",EDGE,"E18.8.0"),sQuery(id+"F0.wireOp",EDGE,"E18.8.1"),sQuery(id+"F0.wireOp",EDGE,"E18.8.2"),sQuery(id+"F0.wireOp",EDGE,"E18.9.0"),sQuery(id+"F0.wireOp",EDGE,"E18.9.1"),sQuery(id+"F0.wireOp",EDGE,"E18.9.2"),sQuery(id+"F0.wireOp",EDGE,"E18.10.0"),sQuery(id+"F0.wireOp",EDGE,"E18.10.1"),sQuery(id+"F0.wireOp",EDGE,"E18.10.2"),sQuery(id+"F0.wireOp",EDGE,"E18.11.0"),sQuery(id+"F0.wireOp",EDGE,"E18.11.1"),sQuery(id+"F0.wireOp",EDGE,"E18.11.2"),sQuery(id+"F0.wireOp",EDGE,"E18.12.0"),sQuery(id+"F0.wireOp",EDGE,"E18.12.1"),sQuery(id+"F0.wireOp",EDGE,"E18.12.2"),sQuery(id+"F0.wireOp",EDGE,"E18.13.0"),sQuery(id+"F0.wireOp",EDGE,"E18.13.1"),sQuery(id+"F0.wireOp",EDGE,"E18.13.2"),sQuery(id+"F0.wireOp",EDGE,"E18.14.0"),sQuery(id+"F0.wireOp",EDGE,"E18.14.1"),sQuery(id+"F0.wireOp",EDGE,"E18.14.2"),subQ0])],"isStart":false})}),makeQuery(id+"F10.opExtrude","SWEPT_FACE",FACE,{"disambiguationData":[OSD([sQuery(id+"F9.wireOp",EDGE,"E23.2.0")])]})]});}
            var Q18;
            {var subQ0=sQuery(id+"F0.wireOp",EDGE,"E18.14.2");var subQ1=sQuery(id+"F0.wireOp",EDGE,"E18.14.1");var subQ2=sQuery(id+"F0.wireOp",EDGE,"E18.14.0");var subQ3=sQuery(id+"F0.wireOp",EDGE,"E18.13.2");var subQ4=sQuery(id+"F0.wireOp",EDGE,"E18.13.1");var subQ5=sQuery(id+"F0.wireOp",EDGE,"E18.13.0");var subQ6=sQuery(id+"F0.wireOp",EDGE,"E18.12.2");var subQ7=sQuery(id+"F0.wireOp",EDGE,"E18.12.1");var subQ8=sQuery(id+"F0.wireOp",EDGE,"E18.12.0");var subQ9=sQuery(id+"F0.wireOp",EDGE,"E18.11.2");var subQ10=sQuery(id+"F0.wireOp",EDGE,"E18.11.1");var subQ11=sQuery(id+"F0.wireOp",EDGE,"E18.11.0");var subQ12=sQuery(id+"F0.wireOp",EDGE,"E18.10.2");var subQ13=sQuery(id+"F0.wireOp",EDGE,"E18.10.1");var subQ14=sQuery(id+"F0.wireOp",EDGE,"E18.10.0");var subQ15=sQuery(id+"F0.wireOp",EDGE,"E18.9.2");var subQ16=sQuery(id+"F0.wireOp",EDGE,"E18.9.1");var subQ17=sQuery(id+"F0.wireOp",EDGE,"E18.9.0");var subQ18=sQuery(id+"F0.wireOp",EDGE,"E18.8.2");var subQ19=sQuery(id+"F0.wireOp",EDGE,"E18.8.1");var subQ20=sQuery(id+"F0.wireOp",EDGE,"E18.8.0");var subQ21=sQuery(id+"F0.wireOp",EDGE,"E18.7.2");var subQ22=sQuery(id+"F0.wireOp",EDGE,"E18.7.1");var subQ23=sQuery(id+"F0.wireOp",EDGE,"E18.7.0");var subQ24=sQuery(id+"F0.wireOp",EDGE,"E18.6.2");var subQ25=sQuery(id+"F0.wireOp",EDGE,"E18.6.1");var subQ26=sQuery(id+"F0.wireOp",EDGE,"E18.6.0");var subQ27=sQuery(id+"F0.wireOp",EDGE,"E18.5.2");var subQ28=sQuery(id+"F0.wireOp",EDGE,"E18.5.1");var subQ29=sQuery(id+"F0.wireOp",EDGE,"E18.5.0");var subQ30=sQuery(id+"F0.wireOp",EDGE,"E18.4.2");var subQ31=sQuery(id+"F0.wireOp",EDGE,"E18.4.1");var subQ32=sQuery(id+"F0.wireOp",EDGE,"E18.4.0");var subQ33=sQuery(id+"F0.wireOp",EDGE,"E18.3.2");var subQ34=sQuery(id+"F0.wireOp",EDGE,"E18.3.1");var subQ35=sQuery(id+"F0.wireOp",EDGE,"E18.3.0");var subQ36=sQuery(id+"F0.wireOp",EDGE,"E18.2.2");var subQ37=sQuery(id+"F0.wireOp",EDGE,"E18.2.1");var subQ38=sQuery(id+"F0.wireOp",EDGE,"E18.2.0");var subQ39=sQuery(id+"F0.wireOp",EDGE,"E18.1.2");var subQ40=sQuery(id+"F0.wireOp",EDGE,"E18.1.1");var subQ41=sQuery(id+"F0.wireOp",EDGE,"E18.1.0");var subQ42=sQuery(id+"F0.wireOp",EDGE,"E14.MirrorC");var subQ43=sQuery(id+"F0.wireOp",EDGE,"E13");var subQ44=sQuery(id+"F0.wireOp",EDGE,"E12");var subQ45=sQuery(id+"F0.wireOp",EDGE,"E0");Q18=makeQuery(id+"F10.boolean.opBoolean","INTERSECT",EDGE,{"derivedFrom":[makeQuery(id+"F6.boolean.opBoolean","MERGE",FACE,{"derivedFrom":[makeQuery(id+"F1.opExtrude","CAP_FACE",FACE,{"disambiguationData":[OSD([subQ45,sQuery(id+"F0.wireOp",EDGE,"E9.5.0"),sQuery(id+"F0.wireOp",EDGE,"E9.5.1"),sQuery(id+"F0.wireOp",EDGE,"E1"),sQuery(id+"F0.wireOp",EDGE,"E9.5.3"),sQuery(id+"F0.wireOp",EDGE,"E9.5.4"),sQuery(id+"F0.wireOp",EDGE,"E8.trimOffspring"),sQuery(id+"F0.wireOp",EDGE,"E9.6.0"),sQuery(id+"F0.wireOp",EDGE,"E9.6.1"),sQuery(id+"F0.wireOp",EDGE,"E9.6.2"),sQuery(id+"F0.wireOp",EDGE,"E9.6.3"),sQuery(id+"F0.wireOp",EDGE,"E9.6.4"),sQuery(id+"F0.wireOp",EDGE,"E9.6.5"),sQuery(id+"F0.wireOp",EDGE,"E9.7.0"),sQuery(id+"F0.wireOp",EDGE,"E9.7.1"),sQuery(id+"F0.wireOp",EDGE,"E9.7.2"),sQuery(id+"F0.wireOp",EDGE,"E9.7.3"),sQuery(id+"F0.wireOp",EDGE,"E9.7.4"),sQuery(id+"F0.wireOp",EDGE,"E9.7.5"),sQuery(id+"F0.wireOp",EDGE,"E9.8.0"),sQuery(id+"F0.wireOp",EDGE,"E9.8.1"),sQuery(id+"F0.wireOp",EDGE,"E9.8.2"),sQuery(id+"F0.wireOp",EDGE,"E9.8.3"),sQuery(id+"F0.wireOp",EDGE,"E9.8.4"),sQuery(id+"F0.wireOp",EDGE,"E9.8.5"),sQuery(id+"F0.wireOp",EDGE,"E9.9.0"),sQuery(id+"F0.wireOp",EDGE,"E9.9.1"),sQuery(id+"F0.wireOp",EDGE,"E9.9.2"),sQuery(id+"F0.wireOp",EDGE,"E9.9.3"),sQuery(id+"F0.wireOp",EDGE,"E9.9.4"),sQuery(id+"F0.wireOp",EDGE,"E9.9.5"),subQ44,subQ43,subQ42,subQ41,subQ40,subQ39,subQ38,subQ37,subQ36,subQ35,subQ34,subQ33,subQ32,subQ31,subQ30,subQ29,subQ28,subQ27,subQ26,subQ25,subQ24,subQ23,subQ22,subQ21,subQ20,subQ19,subQ18,subQ17,subQ16,subQ15,subQ14,subQ13,subQ12,subQ11,subQ10,subQ9,subQ8,subQ7,subQ6,subQ5,subQ4,subQ3,subQ2,subQ1,subQ0,sQuery(id+"F0.wireOp",EDGE,"E19")])],"isStart":true}),makeQuery(id+"F6.opExtrude","CAP_FACE",FACE,{"disambiguationData":[OSD([subQ45,subQ44,subQ43,subQ42,subQ41,subQ40,subQ39,subQ38,subQ37,subQ36,subQ35,subQ34,subQ33,subQ32,subQ31,subQ30,subQ29,subQ28,subQ27,subQ26,subQ25,subQ24,subQ23,subQ22,subQ21,subQ20,subQ19,subQ18,subQ17,subQ16,subQ15,subQ14,subQ13,subQ12,subQ11,subQ10,subQ9,subQ8,subQ7,subQ6,subQ5,subQ4,subQ3,subQ2,subQ1,subQ0,sQuery(id+"F0.wireOp",EDGE,"E20")])],"isStart":true})]}),makeQuery(id+"F10.opExtrude","SWEPT_FACE",FACE,{"disambiguationData":[OSD([sQuery(id+"F9.wireOp",EDGE,"E23.1.0")])]})]});}
            var Q19;
            {var subQ0=sQuery(id+"F0.wireOp",EDGE,"E20");Q19=makeQuery(id+"F10.boolean.opBoolean","INTERSECT",EDGE,{"derivedFrom":[makeQuery(id+"F6.boolean.opBoolean","SPLIT",FACE,{"disambiguationData":[TD([makeQuery(id+"F5.boolean.opBoolean","COPY",FACE,{"derivedFrom":makeQuery(id+"F5.opExtrude","SWEPT_FACE",FACE,{"disambiguationData":[OSD([sQuery(id+"F4.wireOp",EDGE,"E21")])]})})])],"derivedFrom":makeQuery(id+"F6.opExtrude","CAP_FACE",FACE,{"disambiguationData":[OSD([sQuery(id+"F0.wireOp",EDGE,"E0"),sQuery(id+"F0.wireOp",EDGE,"E12"),sQuery(id+"F0.wireOp",EDGE,"E13"),sQuery(id+"F0.wireOp",EDGE,"E14.MirrorC"),sQuery(id+"F0.wireOp",EDGE,"E18.1.0"),sQuery(id+"F0.wireOp",EDGE,"E18.1.1"),sQuery(id+"F0.wireOp",EDGE,"E18.1.2"),sQuery(id+"F0.wireOp",EDGE,"E18.2.0"),sQuery(id+"F0.wireOp",EDGE,"E18.2.1"),sQuery(id+"F0.wireOp",EDGE,"E18.2.2"),sQuery(id+"F0.wireOp",EDGE,"E18.3.0"),sQuery(id+"F0.wireOp",EDGE,"E18.3.1"),sQuery(id+"F0.wireOp",EDGE,"E18.3.2"),sQuery(id+"F0.wireOp",EDGE,"E18.4.0"),sQuery(id+"F0.wireOp",EDGE,"E18.4.1"),sQuery(id+"F0.wireOp",EDGE,"E18.4.2"),sQuery(id+"F0.wireOp",EDGE,"E18.5.0"),sQuery(id+"F0.wireOp",EDGE,"E18.5.1"),sQuery(id+"F0.wireOp",EDGE,"E18.5.2"),sQuery(id+"F0.wireOp",EDGE,"E18.6.0"),sQuery(id+"F0.wireOp",EDGE,"E18.6.1"),sQuery(id+"F0.wireOp",EDGE,"E18.6.2"),sQuery(id+"F0.wireOp",EDGE,"E18.7.0"),sQuery(id+"F0.wireOp",EDGE,"E18.7.1"),sQuery(id+"F0.wireOp",EDGE,"E18.7.2"),sQuery(id+"F0.wireOp",EDGE,"E18.8.0"),sQuery(id+"F0.wireOp",EDGE,"E18.8.1"),sQuery(id+"F0.wireOp",EDGE,"E18.8.2"),sQuery(id+"F0.wireOp",EDGE,"E18.9.0"),sQuery(id+"F0.wireOp",EDGE,"E18.9.1"),sQuery(id+"F0.wireOp",EDGE,"E18.9.2"),sQuery(id+"F0.wireOp",EDGE,"E18.10.0"),sQuery(id+"F0.wireOp",EDGE,"E18.10.1"),sQuery(id+"F0.wireOp",EDGE,"E18.10.2"),sQuery(id+"F0.wireOp",EDGE,"E18.11.0"),sQuery(id+"F0.wireOp",EDGE,"E18.11.1"),sQuery(id+"F0.wireOp",EDGE,"E18.11.2"),sQuery(id+"F0.wireOp",EDGE,"E18.12.0"),sQuery(id+"F0.wireOp",EDGE,"E18.12.1"),sQuery(id+"F0.wireOp",EDGE,"E18.12.2"),sQuery(id+"F0.wireOp",EDGE,"E18.13.0"),sQuery(id+"F0.wireOp",EDGE,"E18.13.1"),sQuery(id+"F0.wireOp",EDGE,"E18.13.2"),sQuery(id+"F0.wireOp",EDGE,"E18.14.0"),sQuery(id+"F0.wireOp",EDGE,"E18.14.1"),sQuery(id+"F0.wireOp",EDGE,"E18.14.2"),subQ0])],"isStart":false})}),makeQuery(id+"F10.opExtrude","SWEPT_FACE",FACE,{"disambiguationData":[OSD([sQuery(id+"F9.wireOp",EDGE,"E23.1.0")])]})]});}
            chamfer(context, id + "F11", {"entities" : qUnion([Q0, Q1, Q2, Q3, Q4, Q5, Q6, Q7, Q8, Q9, Q10, Q11, Q12, Q13, Q14, Q15, Q16, Q17, Q18, Q19]), "width" : 1 * mm, "tangentPropagation" : true});
        }
    });
